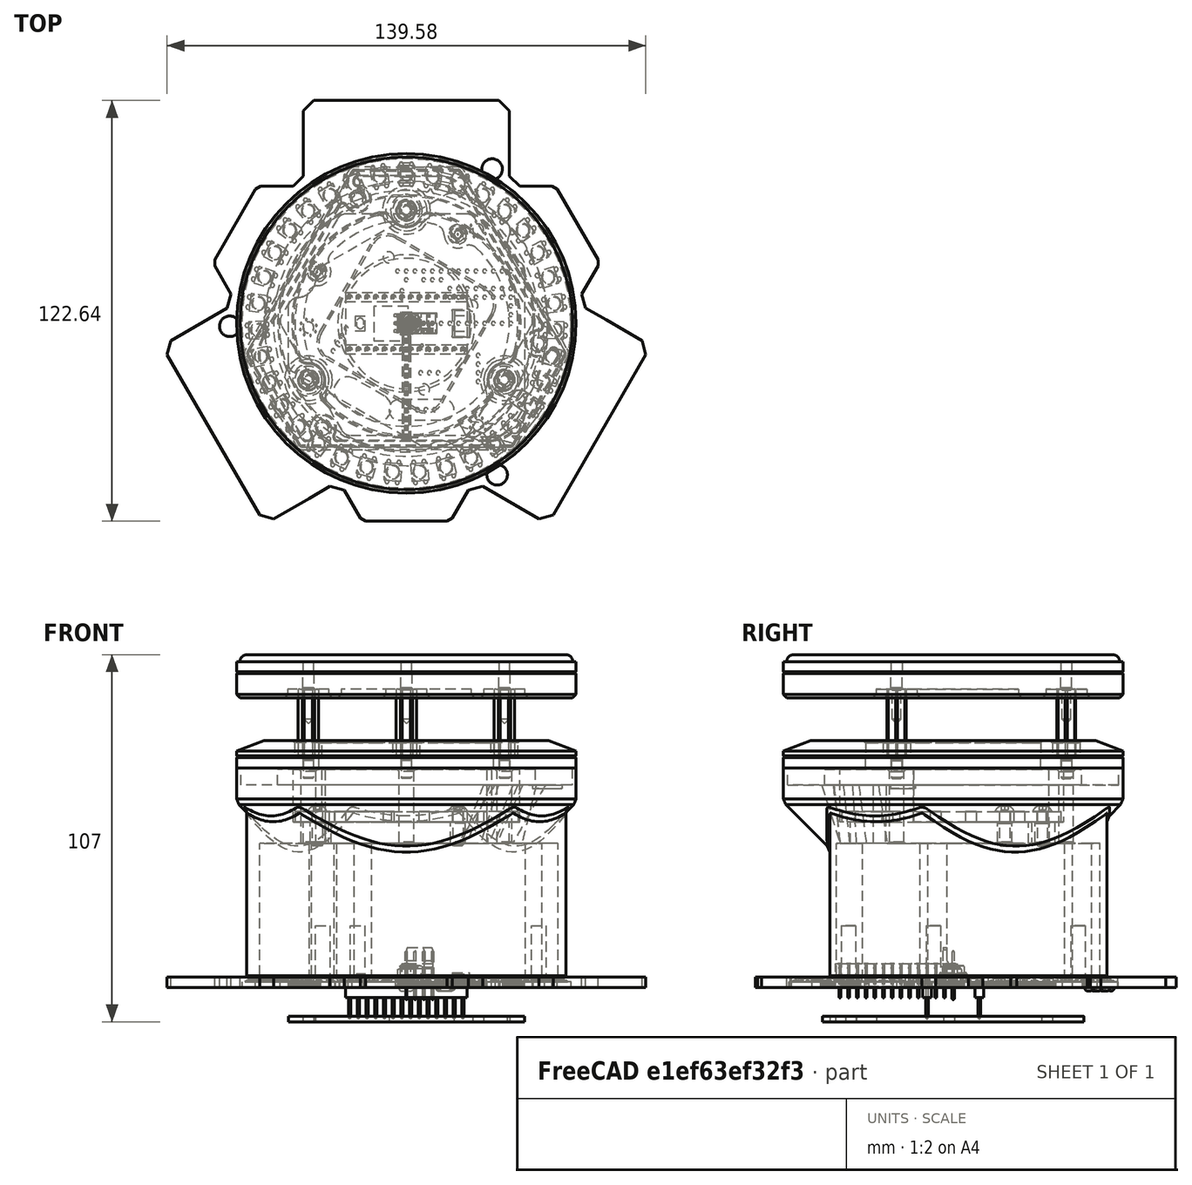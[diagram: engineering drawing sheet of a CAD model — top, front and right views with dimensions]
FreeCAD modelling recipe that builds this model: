
FCSTD DOCUMENT  (FreeCAD 2024.1006R14555 (Git shallow))
Label: beacon_assembled
License: Creative Commons Attribution-NoDerivatives
LicenseURL: http://creativecommons.org/licenses/by-nd/4.0/
objects: Sketcher::SketchObject×35, App::Part×19, PartDesign::Pocket×18, Part::Feature×17, PartDesign::Pad×14, PartDesign::Fillet×14, PartDesign::Chamfer×13, PartDesign::Body×11, Part::FeaturePython×5, PartDesign::PolarPattern×4, PartDesign::SubShapeBinder×4, PartDesign::AuxGroup×3, Part::SubShapeBinder×2, Sketcher::SketchExport×2, App::Link×1, PartDesign::Revolution×1, App::DocumentObjectGroup×1, TechDraw::DrawSVGTemplate×1, TechDraw::DrawProjGroupItem×1, TechDraw::DrawProjGroup×1, +3 more types
note: 307 computed .brp shape members not serialized (recipe doc carries the construction recipe); baked Part::Feature solids carry a one-line shape summary decoded from their .brp
EXTERNAL_REF file=../mechanical-parts/generic-hardware.FCStd obj=Part003
EXTERNAL_REF file=../table_2022.FCStd obj=Group
EXTERNAL_REF file=../robot_holonome.FCStd obj=Part

FEATURE [Sketcher::SketchObject] Sketch
  ArcFitTolerance = 0
  AttachmentSupport = -> [XY_Plane]
  ExternalBSplineMaxDegree = 0
  ExternalBSplineTolerance = 0
  FullyConstrained = true
  InternalTolerance = 1e-06
  InvalidShape = false
  MakeInternals = false
  MapMode = 5
  Support = -> [XY_Plane]
  TreeRank = 0
  ValidateShape = true
  sketch-geometry (17):
    g0: LineSegment StartX=0 StartY=0 StartZ=0 EndX=-49.9177 EndY=28.82 EndZ=0
    g1: LineSegment StartX=-49.9177 StartY=28.82 StartZ=0 EndX=-56.3725 EndY=17.64 EndZ=0
    g2: LineSegment StartX=-56.3725 StartY=17.64 StartZ=0 EndX=-49.641 EndY=5.98076 EndZ=0
    g3: LineSegment StartX=-49.641 StartY=5.98076 StartZ=0 EndX=-58.3013 EndY=0.980762 EndZ=0
    g4: LineSegment [constr] StartX=-58.3013 StartY=0.980762 StartZ=0 EndX=-28.3013 EndY=-50.9808 EndZ=0
    g5: LineSegment StartX=-28.3013 StartY=-50.9808 StartZ=0 EndX=-19.641 EndY=-45.9808 EndZ=0
    g6: LineSegment StartX=-19.641 StartY=-45.9808 StartZ=0 EndX=-12.9096 EndY=-57.64 EndZ=0
    g7: LineSegment StartX=-12.9096 StartY=-57.64 StartZ=0 EndX=0 EndY=-57.64 EndZ=0
    g8: LineSegment StartX=0 StartY=-57.64 StartZ=0 EndX=0 EndY=0 EndZ=0
    g9: LineSegment [constr] StartX=-49.641 StartY=5.98076 StartZ=0 EndX=-19.641 EndY=-45.9808 EndZ=0
    g10: LineSegment [constr] StartX=0 StartY=0 StartZ=0 EndX=-43.3013 EndY=-25 EndZ=0
    g11: LineSegment [constr] StartX=-53.9711 StartY=3.48076 StartZ=0 EndX=-23.9711 EndY=-48.4808 EndZ=0
    g12: Circle CenterX=-51.4711 CenterY=-0.849365 CenterZ=0 NormalX=0 NormalY=0 NormalZ=1 AngleXU=0 Radius=1.6
    g13: Circle [constr] CenterX=-26.4711 CenterY=-44.1506 CenterZ=0 NormalX=0 NormalY=0 NormalZ=1 AngleXU=0 Radius=1.6
    g14: LineSegment StartX=-58.3013 StartY=0.980762 StartZ=0 EndX=-71.2917 EndY=-6.51924 EndZ=0
    g15: LineSegment StartX=-71.2917 StartY=-6.51924 StartZ=0 EndX=-41.2917 EndY=-58.4808 EndZ=0
    g16: LineSegment StartX=-41.2917 StartY=-58.4808 StartZ=0 EndX=-28.3013 EndY=-50.9808 EndZ=0
  constraints (47):
    c: Coincident(g0,g-1)
    c: Coincident(g0,g1)
    c: Coincident(g1,g2)
    c: Coincident(g2,g3)
    c: Coincident(g3,g4)
    c: Coincident(g4,g5)
    c: Coincident(g5,g6)
    c: Coincident(g6,g7)
    c: PointOnObject(g7,g-2)
    c: Horizontal(g7)
    c: Coincident(g7,g8)
    c: Coincident(g8,g0)
    c: Equal(g0,g8)
    c: Angle(g0,g8) = 2.0944
    c: Perpendicular(g0,g1)
    c: Equal(g1,g7)
    c: Perpendicular(g3,g2)
    c: Perpendicular(g3,g4)
    c: Perpendicular(g5,g4)
    c: Coincident(g9,g2)
    c: Coincident(g9,g5)
    c: Coincident(g10,g0)
    c: PointOnObject(g10,g4)
    c: Parallel(g2,g9)
    c: Parallel(g9,g6)
    c: Distance(g4) = 60
    c: Distance(g3) = 10
    c: Perpendicular(g4,g10)
    c: Distance(g0,g9) = 40
    c: PointOnObject(g11,g5)
    c: Symmetric(g3,g2,g11)
    c: PointOnObject(g12,g11)
    c: PointOnObject(g13,g11)
    c: Diameter(g13) = 3.2
    c: Equal(g13,g12)
    c: Symmetric(g13,g12,g10)
    c: Distance(g12,g3) = 5
    c: Coincident(g14,g3)
    c: Coincident(g14,g15)
    c: Coincident(g15,g16)
    c: Coincident(g16,g4)
    c: Parallel(g16,g5)
    c: Parallel(g3,g14)
    c: Parallel(g15,g4)
    c: Distance(g14) = 15
    c: Equal(g6,g2)
    c: DistanceY(g8,g8) = 57.64
FEATURE [PartDesign::Pad] Pad
  AddSubType = 0
  AutoTaperInnerAngle = false
  CheckUpToFaceLimits = true
  ClaimChildren = false
  Direction = (0,0,1)
  Fit = 0
  FitJoin = 0
  InnerFit = 0
  InnerFitJoin = 0
  InvalidShape = false
  Length = 3
  Length2 = 100
  Linearize = true
  NewSolid = false
  Profile = -> Sketch
  Refine = true
  Suppress = false
  TaperInnerAngle = 0
  TaperInnerAngleRev = 0
  TreeRank = 0
  Type = 0
  ValidateShape = true
  _ProfileBasedVersion = 1
FEATURE [PartDesign::PolarPattern] PolarPattern
  AddSubType = 0
  Angle = 360
  Axis = -> Sketch [N_Axis]
  BaseFeature = -> Pad
  CopyShape = false
  HideBaseFeature = false
  InvalidShape = false
  NewSolid = false
  Occurrences = 3
  OffsetBaseFeature = true
  OriginalSubs = -> [Pad]
  Originals = -> [Pad]
  ParallelTransform = true
  Refine = true
  SubTransform = true
  Suppress = false
  TreeRank = 0
  ValidateShape = true
  _Version = 3
FEATURE [Sketcher::SketchObject] Sketch001
  ArcFitTolerance = 0
  AttachmentSupport = -> [XY_Plane]
  ExternalBSplineMaxDegree = 0
  ExternalBSplineTolerance = 0
  ExternalGeometry = -> [PolarPattern]
  FullyConstrained = false
  InternalTolerance = 1e-06
  InvalidShape = false
  MakeInternals = false
  MapMode = 5
  Support = -> [XY_Plane]
  TreeRank = 0
  ValidateShape = true
  sketch-geometry (6):
    g0: LineSegment StartX=-28.2671 StartY=16.32 StartZ=0 EndX=-37.2671 EndY=0.731543 EndZ=0
    g1: LineSegment StartX=-37.2671 StartY=0.731543 StartZ=0 EndX=-18 EndY=-32.64 EndZ=0
    g2: LineSegment StartX=-18 StartY=-32.64 StartZ=0 EndX=0 EndY=-32.64 EndZ=0
    g3: LineSegment StartX=-28.2671 StartY=16.32 StartZ=0 EndX=0 EndY=0 EndZ=0
    g4: LineSegment StartX=0 StartY=0 StartZ=0 EndX=0 EndY=-32.64 EndZ=0
    g5: LineSegment [constr] StartX=0 StartY=0 StartZ=0 EndX=-46.3654 EndY=26.7691 EndZ=0
  constraints (16):
    c: Coincident(g0,g1)
    c: Coincident(g1,g2)
    c: Horizontal(g2)
    c: Equal(g2,g0)
    c: Coincident(g0,g3)
    c: Coincident(g3,g4)
    c: Coincident(g4,g2)
    c: DistanceX(g2,g2) = 18
    c: Coincident(g5,g3)
    c: PointOnObject(g0,g5)
    c: Equal(g3,g4)
    c: Coincident(g3,g-1)
    c: Parallel(g-3,g1)
    c: DistanceY(g-5,g2) = 25
    c: Parallel(g0,g-4)
    c: PointOnObject(g2,g-2)
FEATURE [PartDesign::Pocket] Pocket
  AddSubType = 1
  AutoTaperInnerAngle = false
  BaseFeature = -> PolarPattern
  CheckUpToFaceLimits = true
  ClaimChildren = false
  Direction = (0,0,-1)
  Fit = 0
  FitJoin = 0
  InnerFit = 0
  InnerFitJoin = 0
  InvalidShape = false
  Length = 5
  Length2 = 100
  Linearize = true
  NewSolid = false
  Profile = -> Sketch001
  Refine = true
  Reversed = true
  Suppress = false
  TaperInnerAngle = 0
  TaperInnerAngleRev = 0
  TreeRank = 0
  Type = 1
  ValidateShape = true
  _ProfileBasedVersion = 1
  _Version = 1
FEATURE [PartDesign::PolarPattern] PolarPattern001
  AddSubType = 0
  Angle = 360
  Axis = -> Sketch001 [N_Axis]
  BaseFeature = -> Pocket
  CopyShape = false
  HideBaseFeature = false
  InvalidShape = false
  NewSolid = false
  Occurrences = 3
  OffsetBaseFeature = true
  OriginalSubs = -> [Pocket]
  Originals = -> [Pocket]
  ParallelTransform = true
  Refine = true
  SubTransform = true
  Suppress = false
  TreeRank = 0
  ValidateShape = true
  _Version = 3
FEATURE [PartDesign::Chamfer] Chamfer
  AddSubType = 0
  Angle = 45
  Base = -> PolarPattern001 [Edge67,Edge68,Edge1,Edge6,Edge75,Edge74]
  BaseFeature = -> PolarPattern001
  ChamferType = 0
  FlipDirection = false
  InvalidShape = false
  NewSolid = false
  Refine = true
  Size = 1
  Size2 = 1
  SupportTransform = false
  Suppress = false
  TreeRank = 0
  UseAllEdges = false
  ValidateShape = true
FEATURE [PartDesign::Fillet] Fillet
  AddSubType = 0
  Base = -> Chamfer [Edge98,Edge102,Edge103,Edge101,Edge100,Edge99]
  BaseFeature = -> Chamfer
  InvalidShape = false
  NewSolid = false
  Radius = 3
  Refine = true
  SupportTransform = false
  Suppress = false
  TreeRank = 0
  UseAllEdges = false
  ValidateShape = true
FEATURE [App::Link] Link001  label="Link001(LD06)"
  AutoLinkLabel = true
  AutoPlacement = true
  LinkPlacement = pos=(2.4274e-12,-2.45859e-11,51.3) rot=(0,0,-1;0.523599rad)
  LinkedObject = -> <external ../mechanical-parts/generic-hardware.FCStd>#Part003
  Placement = pos=(2.4274e-12,-2.45859e-11,51.3) rot=(0,0,-1;0.523599rad)
  SyncGroupVisibility = false
  TreeRank = 83
  _LinkVersion = 1
FEATURE [Part::FeaturePython] PcbStandoff  label="M3x5.5x20-Standoff"  # WARN: FeaturePython — macro-defined, semantics opaque (R4)
  Diameter = 2
  InvalidShape = false
  Invert = false
  LeftHanded = false
  Length = 2
  LengthCustom = 20
  MatchOuter = false
  OffsetAngle = 0
  Placement = pos=(-28.5788,-16.5,67) rot=(0,0,1;0rad)
  ScrewLength = 6
  Thread = false
  TreeRank = 174
  Type = 0
  ValidateShape = true
  Width = 1
FEATURE [Part::FeaturePython] PcbStandoff001  label="M3x5.5x20-Standoff001"  # WARN: FeaturePython — macro-defined, semantics opaque (R4)
  Diameter = 2
  InvalidShape = false
  Invert = false
  LeftHanded = false
  Length = 2
  LengthCustom = 20
  MatchOuter = false
  OffsetAngle = 0
  Placement = pos=(28.5788,-16.5,67) rot=(0,0,1;0rad)
  ScrewLength = 6
  Thread = false
  TreeRank = 175
  Type = 0
  ValidateShape = true
  Width = 1
FEATURE [Part::FeaturePython] PcbStandoff002  label="M3x5.5x20-Standoff002"  # WARN: FeaturePython — macro-defined, semantics opaque (R4)
  Diameter = 2
  InvalidShape = false
  Invert = false
  LeftHanded = false
  Length = 2
  LengthCustom = 20
  MatchOuter = false
  OffsetAngle = 0
  Placement = pos=(1.974e-13,33,67) rot=(0,0,1;0rad)
  ScrewLength = 6
  Thread = false
  TreeRank = 176
  Type = 0
  ValidateShape = true
  Width = 1
FEATURE [Sketcher::SketchObject] Sketch042
  ArcFitTolerance = 0
  AttachmentSupport = -> [XY_Plane024]
  ExternalBSplineMaxDegree = 0
  ExternalBSplineTolerance = 0
  FullyConstrained = true
  InternalTolerance = 1e-06
  InvalidShape = false
  MakeInternals = false
  MapMode = 5
  Support = -> [XY_Plane024]
  TreeRank = 402
  ValidateShape = true
  sketch-geometry (9):
    g0: LineSegment StartX=-15.683 StartY=44.8363 StartZ=0 EndX=15.683 EndY=44.8363 EndZ=0
    g1: Circle [constr] CenterX=-4.0211e-12 CenterY=3.5659e-12 CenterZ=0 NormalX=0 NormalY=0 NormalZ=1 AngleXU=0 Radius=47.5
    g2: Circle [constr] CenterX=-4.0211e-12 CenterY=3.5659e-12 CenterZ=0 NormalX=0 NormalY=0 NormalZ=1 AngleXU=0 Radius=36
    g3: LineSegment StartX=-15.683 StartY=44.8363 StartZ=0 EndX=-46.6709 EndY=-8.83631 EndZ=0
    g4: LineSegment StartX=-46.6709 StartY=-8.83631 StartZ=0 EndX=-30.9879 EndY=-36 EndZ=0
    g5: LineSegment StartX=-30.9879 StartY=-36 StartZ=0 EndX=30.9879 EndY=-36 EndZ=0
    g6: LineSegment StartX=30.9879 StartY=-36 StartZ=0 EndX=46.6709 EndY=-8.83631 EndZ=0
    g7: LineSegment StartX=46.6709 StartY=-8.83631 StartZ=0 EndX=15.683 EndY=44.8363 EndZ=0
    g8: LineSegment [constr] StartX=-4.0211e-12 StartY=3.5659e-12 StartZ=0 EndX=-38.8294 EndY=-22.4182 EndZ=0
  constraints (25):
    c: Horizontal(g0)
    c: PointOnObject(g0,g1)
    c: Diameter(g1) = 95
    c: PointOnObject(g0,g1)
    c: Diameter(g2) = 72
    c: Coincident(g3,g0)
    c: PointOnObject(g3,g1)
    c: Coincident(g2,g1)
    c: Coincident(g2,g-1)
    c: Coincident(g4,g3)
    c: PointOnObject(g4,g1)
    c: Coincident(g5,g4)
    c: PointOnObject(g5,g1)
    c: Horizontal(g5)
    c: Coincident(g6,g5)
    c: PointOnObject(g6,g1)
    c: Coincident(g7,g6)
    c: Coincident(g7,g0)
    c: Equal(g0,g4)
    c: Equal(g4,g6)
    c: Equal(g7,g5)
    c: Coincident(g8,g2)
    c: PointOnObject(g8,g4)
    c: Perpendicular(g4,g8)
    c: Tangent(g5,g2)
FEATURE [PartDesign::Pad] Pad026
  AddSubType = 0
  AlongSketchNormal = false
  AutoTaperInnerAngle = false
  CheckUpToFaceLimits = true
  ClaimChildren = false
  Direction = (0,0,1)
  Fit = 0
  FitJoin = 0
  InnerFit = 0
  InnerFitJoin = 0
  InvalidShape = false
  Length = 61
  Length2 = 100
  Linearize = true
  NewSolid = false
  Profile = -> Sketch042
  Refine = true
  Suppress = false
  TaperInnerAngle = 0
  TaperInnerAngleRev = 0
  TreeRank = 403
  Type = 0
  ValidateShape = true
  _ProfileBasedVersion = 1
FEATURE [Sketcher::SketchObject] Sketch043
  ArcFitTolerance = 0
  AttachmentSupport = -> [YZ_Plane024]
  ExternalBSplineMaxDegree = 0
  ExternalBSplineTolerance = 0
  ExternalGeometry = -> [Pad026]
  FullyConstrained = true
  InternalTolerance = 1e-06
  InvalidShape = false
  MakeInternals = false
  MapMode = 5
  Placement = pos=(0,0,0) rot=(0.57735,0.57735,0.57735;2.0944rad)
  Support = -> [YZ_Plane024]
  TreeRank = 404
  ValidateShape = true
  sketch-geometry (5):
    g0: LineSegment StartX=-3.572e-13 StartY=61 StartZ=0 EndX=49.5 EndY=61 EndZ=0
    g1: LineSegment StartX=49.5 StartY=61 StartZ=0 EndX=49.5 EndY=51 EndZ=0
    g2: LineSegment StartX=49.5 StartY=51 StartZ=0 EndX=20 EndY=21.5 EndZ=0
    g3: LineSegment StartX=-2.9e-14 StartY=21.5 StartZ=0 EndX=20 EndY=21.5 EndZ=0
    g4: LineSegment StartX=-2.9e-14 StartY=21.5 StartZ=0 EndX=-3.572e-13 EndY=61 EndZ=0
  constraints (15):
    c: PointOnObject(g0,g-2)
    c: Horizontal(g0)
    c: Coincident(g1,g0)
    c: Coincident(g2,g1)
    c: PointOnObject(g3,g-2)
    c: Coincident(g3,g2)
    c: Horizontal(g3)
    c: Coincident(g4,g0)
    c: Coincident(g3,g4)
    c: Vertical(g1)
    c: PointOnObject(g-3,g0)
    c: DistanceY(g1,g1) = 10
    c: Angle(g1,g2) = 2.35619
    c: DistanceX(g0,g0) = 49.5
    c: DistanceX(g3,g3) = 20
FEATURE [PartDesign::Revolution] Revolution004
  AddSubType = 0
  Angle = 360
  Axis = (-2e-16,3e-16,1)
  Base = (0,0,0)
  BaseFeature = -> Pad026
  ClaimChildren = false
  Fit = 0
  FitJoin = 0
  InnerFit = 0
  InnerFitJoin = 0
  InvalidShape = false
  Linearize = true
  NewSolid = false
  Profile = -> Sketch043
  ReferenceAxis = -> Sketch043 [V_Axis]
  Refine = true
  Reversed = true
  Suppress = false
  TreeRank = 405
  ValidateShape = true
  _ProfileBasedVersion = 1
FEATURE [Sketcher::SketchObject] Sketch044
  ArcFitTolerance = 0
  AttachmentSupport = -> [Revolution004]
  ExternalBSplineMaxDegree = 0
  ExternalBSplineTolerance = 0
  FullyConstrained = true
  InternalTolerance = 1e-06
  InvalidShape = false
  MakeInternals = false
  MapMode = 5
  Placement = pos=(-1.34e-14,1.71e-14,61) rot=(0,0,1;0rad)
  Support = -> [Revolution004]
  TreeRank = 406
  ValidateShape = true
  sketch-geometry (2):
    g0: Circle CenterX=0 CenterY=0 CenterZ=0 NormalX=0 NormalY=0 NormalZ=1 AngleXU=0 Radius=48.25
    g1: Circle CenterX=0 CenterY=0 CenterZ=0 NormalX=0 NormalY=0 NormalZ=1 AngleXU=0 Radius=37.5
  constraints (4):
    c: Coincident(g0,g-1)
    c: Coincident(g1,g0)
    c: Diameter(g0) = 96.5
    c: Diameter(g1) = 75
FEATURE [PartDesign::Pocket] Pocket019
  AddSubType = 1
  AutoTaperInnerAngle = false
  BaseFeature = -> Revolution004
  CheckUpToFaceLimits = true
  ClaimChildren = false
  Direction = (1,1,1)
  Fit = 0
  FitJoin = 0
  InnerFit = 0
  InnerFitJoin = 0
  InvalidShape = false
  Length = 5
  Length2 = 100
  Linearize = true
  NewSolid = false
  Profile = -> Sketch044
  Refine = true
  Suppress = false
  TaperInnerAngle = 0
  TaperInnerAngleRev = 0
  TreeRank = 407
  Type = 0
  ValidateShape = true
  _ProfileBasedVersion = 1
  _Version = 1
FEATURE [Sketcher::SketchObject] Sketch045
  ArcFitTolerance = 0
  AttachmentSupport = -> [Pocket019]
  ExternalBSplineMaxDegree = 0
  ExternalBSplineTolerance = 0
  FullyConstrained = true
  InternalTolerance = 1e-06
  InvalidShape = false
  MakeInternals = false
  MapMode = 5
  Placement = pos=(-1.34e-14,1.71e-14,61) rot=(0,0,1;0rad)
  Support = -> [Pocket019]
  TreeRank = 408
  ValidateShape = true
  sketch-geometry (6):
    g0: Circle CenterX=-6.97e-14 CenterY=33 CenterZ=0 NormalX=0 NormalY=0 NormalZ=1 AngleXU=0 Radius=2.1
    g1: Circle CenterX=28.5788 CenterY=-16.5 CenterZ=0 NormalX=0 NormalY=0 NormalZ=1 AngleXU=0 Radius=2.1
    g2: Circle CenterX=-28.5788 CenterY=-16.5 CenterZ=0 NormalX=0 NormalY=0 NormalZ=1 AngleXU=0 Radius=2.1
    g3: LineSegment [constr] StartX=-28.5788 StartY=-16.5 StartZ=0 EndX=4.26e-14 EndY=-1.279e-13 EndZ=0
    g4: LineSegment [constr] StartX=4.18e-14 StartY=-1.265e-13 StartZ=0 EndX=28.5788 EndY=-16.5 EndZ=0
    g5: LineSegment [constr] StartX=4.18e-14 StartY=-1.265e-13 StartZ=0 EndX=-6.97e-14 EndY=33 EndZ=0
  constraints (15):
    c: PointOnObject(g0,g-2)
    c: Coincident(g3,g2)
    c: Coincident(g3,g-1)
    c: Coincident(g4,g3)
    c: Coincident(g4,g1)
    c: Coincident(g5,g3)
    c: Coincident(g5,g0)
    c: Equal(g2,g1)
    c: Equal(g2,g0)
    c: Diameter(g2) = 4.2
    c: Equal(g3,g4)
    c: Equal(g4,g5)
    c: Angle(g4,g5) = 2.0944
    c: Angle(g5,g3) = 2.0944
    c: DistanceY(g5,g5) = 33
FEATURE [PartDesign::Pocket] Pocket020
  AddSubType = 1
  AutoTaperInnerAngle = false
  BaseFeature = -> Pocket019
  CheckUpToFaceLimits = true
  ClaimChildren = false
  Direction = (1,1,1)
  Fit = 0
  FitJoin = 0
  InnerFit = 0
  InnerFitJoin = 0
  InvalidShape = false
  Length = 12
  Length2 = 100
  Linearize = true
  NewSolid = false
  Profile = -> Sketch045
  Refine = true
  Suppress = false
  TaperInnerAngle = 0
  TaperInnerAngleRev = 0
  TreeRank = 409
  Type = 1
  ValidateShape = true
  _ProfileBasedVersion = 1
  _Version = 1
FEATURE [Sketcher::SketchObject] Sketch046
  ArcFitTolerance = 0
  AttachmentSupport = -> [XY_Plane025]
  ExternalBSplineMaxDegree = 0
  ExternalBSplineTolerance = 0
  FullyConstrained = true
  InternalTolerance = 1e-06
  InvalidShape = false
  MakeInternals = false
  MapMode = 5
  Support = -> [XY_Plane025]
  TreeRank = 422
  ValidateShape = true
  sketch-geometry (12):
    g0: Circle CenterX=-1.6806e-12 CenterY=-6.0018e-12 CenterZ=0 NormalX=0 NormalY=0 NormalZ=1 AngleXU=0 Radius=49.5
    g1: LineSegment StartX=-27.3205 StartY=-7.32051 StartZ=0 EndX=-7.32051 EndY=27.3205 EndZ=0
    g2: LineSegment StartX=-7.32051 StartY=27.3205 StartZ=0 EndX=27.3205 EndY=7.32051 EndZ=0
    g3: LineSegment StartX=27.3205 StartY=7.32051 StartZ=0 EndX=7.32051 EndY=-27.3205 EndZ=0
    g4: LineSegment StartX=7.32051 StartY=-27.3205 StartZ=0 EndX=-27.3205 EndY=-7.32051 EndZ=0
    g5: GeomPoint [constr] X=-1.6806e-12 Y=-6.0018e-12 Z=0
    g6: Circle CenterX=1.962e-13 CenterY=33 CenterZ=0 NormalX=0 NormalY=0 NormalZ=1 AngleXU=0 Radius=1.6
    g7: Circle CenterX=28.5788 CenterY=-16.5 CenterZ=0 NormalX=0 NormalY=0 NormalZ=1 AngleXU=0 Radius=1.6
    g8: Circle CenterX=-28.5788 CenterY=-16.5 CenterZ=0 NormalX=0 NormalY=0 NormalZ=1 AngleXU=0 Radius=1.6
    g9: LineSegment [constr] StartX=-28.5788 StartY=-16.5 StartZ=0 EndX=-1.6804e-12 EndY=-6.0005e-12 EndZ=0
    g10: LineSegment [constr] StartX=-1.6806e-12 StartY=-6.0018e-12 StartZ=0 EndX=28.5788 EndY=-16.5 EndZ=0
    g11: LineSegment [constr] StartX=-1.6806e-12 StartY=-6.0018e-12 StartZ=0 EndX=1.962e-13 EndY=33 EndZ=0
  constraints (29):
    c: Coincident(g0,g-1)
    c: Diameter(g0) = 99
    c: Coincident(g1,g2)
    c: Coincident(g2,g3)
    c: Coincident(g3,g4)
    c: Coincident(g4,g1)
    c: Parallel(g2,g4)
    c: Parallel(g1,g3)
    c: Symmetric(g2,g1,g5)
    c: Coincident(g5,g0)
    c: Perpendicular(g1,g2)
    c: Equal(g3,g2)
    c: Angle(g-2,g4) = 1.0472
    c: Distance(g3) = 40
    c: PointOnObject(g6,g-2)
    c: Equal(g8,g6)
    c: Equal(g8,g7)
    c: Diameter(g8) = 3.2
    c: DistanceY(g0,g6) = 33
    c: Coincident(g9,g8)
    c: Coincident(g9,g0)
    c: Coincident(g10,g0)
    c: Coincident(g10,g7)
    c: Coincident(g11,g0)
    c: Coincident(g11,g6)
    c: Equal(g9,g10)
    c: Equal(g10,g11)
    c: Angle(g10,g11) = 2.0944
    c: Angle(g11,g9) = 2.0944
FEATURE [PartDesign::Pad] Pad027
  AddSubType = 0
  AlongSketchNormal = false
  AutoTaperInnerAngle = false
  CheckUpToFaceLimits = true
  ClaimChildren = false
  Direction = (0,0,1)
  Fit = 0
  FitJoin = 0
  InnerFit = 0
  InnerFitJoin = 0
  InvalidShape = false
  Length = 3
  Length2 = 100
  Linearize = true
  NewSolid = false
  Profile = -> Sketch046
  Refine = true
  Suppress = false
  TaperInnerAngle = 0
  TaperInnerAngleRev = 0
  TreeRank = 423
  Type = 0
  ValidateShape = true
  _ProfileBasedVersion = 1
FEATURE [PartDesign::Fillet] Fillet011
  AddSubType = 0
  Base = -> Pad027 [Edge4,Edge11,Edge8,Edge5]
  BaseFeature = -> Pad027
  InvalidShape = false
  NewSolid = false
  Radius = 5
  Refine = true
  SupportTransform = false
  Suppress = false
  TreeRank = 424
  UseAllEdges = false
  ValidateShape = true
FEATURE [PartDesign::Body] Body024  label="PlaqueDiffuse"
  AutoGroupSolids = false
  ClaimAllChildren = false
  ExportMode = 0
  Group = -> [Sketch046,Pad027,Fillet011]
  InvalidShape = false
  Origin = -> Origin032
  Placement = pos=(0,0,64) rot=(0,0,1;0rad)
  SingleSolid = true
  Tip = -> Fillet011
  TreeRank = 419
  ValidateShape = true
  _ExportChildren = -> [Pad027,Fillet011]
  _GroupVersion = 1
FEATURE [Sketcher::SketchObject] Sketch047
  ArcFitTolerance = 0
  AttachmentSupport = -> [Pocket020]
  ExternalBSplineMaxDegree = 0
  ExternalBSplineTolerance = 0
  ExternalGeometry = -> [Pocket020]
  FullyConstrained = true
  InternalTolerance = 1e-06
  InvalidShape = false
  MakeInternals = false
  MapMode = 5
  Placement = pos=(-1.34e-14,1.71e-14,61) rot=(0,0,1;0rad)
  Support = -> [Pocket020]
  TreeRank = 425
  ValidateShape = true
  sketch-geometry (6):
    g0: ArcOfCircle CenterX=5.9282e-12 CenterY=33 CenterZ=0 NormalX=0 NormalY=0 NormalZ=1 AngleXU=0 Radius=5 StartAngle=3.21742 EndAngle=6.20736
    g1: ArcOfCircle CenterX=-28.5788 CenterY=-16.5 CenterZ=0 NormalX=0 NormalY=0 NormalZ=1 AngleXU=0 Radius=5 StartAngle=5.31182 EndAngle=8.30175
    g2: ArcOfCircle CenterX=28.5788 CenterY=-16.5 CenterZ=0 NormalX=0 NormalY=0 NormalZ=1 AngleXU=0 Radius=5 StartAngle=1.12303 EndAngle=4.11296
    g3: ArcOfCircle CenterX=1.58681e-11 CenterY=6.06976e-11 CenterZ=0 NormalX=0 NormalY=0 NormalZ=1 AngleXU=0 Radius=33 StartAngle=1.72246 EndAngle=3.51353
    g4: ArcOfCircle CenterX=1.58681e-11 CenterY=6.06976e-11 CenterZ=0 NormalX=0 NormalY=0 NormalZ=1 AngleXU=0 Radius=33 StartAngle=5.91125 EndAngle=7.70232
    g5: ArcOfCircle CenterX=1.58681e-11 CenterY=6.06976e-11 CenterZ=0 NormalX=0 NormalY=0 NormalZ=1 AngleXU=0 Radius=33 StartAngle=3.81685 EndAngle=5.60793
  constraints (18):
    c: Coincident(g0,g-3)
    c: Coincident(g1,g-5)
    c: Coincident(g2,g-4)
    c: Coincident(g3,g-1)
    c: Coincident(g3,g1)
    c: Coincident(g3,g0)
    c: Coincident(g4,g3)
    c: Coincident(g4,g0)
    c: Coincident(g4,g2)
    c: Coincident(g5,g3)
    c: Coincident(g5,g1)
    c: Coincident(g5,g2)
    c: Equal(g3,g4)
    c: Equal(g4,g5)
    c: Equal(g0,g2)
    c: Equal(g2,g1)
    c: Radius(g4) = 33
    c: Radius(g2) = 5
FEATURE [PartDesign::Pocket] Pocket021
  AddSubType = 1
  AutoTaperInnerAngle = false
  BaseFeature = -> Pocket020
  CheckUpToFaceLimits = true
  ClaimChildren = false
  Direction = (1,1,1)
  Fit = 0
  FitJoin = 0
  InnerFit = 0
  InnerFitJoin = 0
  InvalidShape = false
  Length = 15.7
  Length2 = 100
  Linearize = true
  NewSolid = false
  Profile = -> Sketch047
  Refine = true
  Suppress = false
  TaperInnerAngle = 0
  TaperInnerAngleRev = 0
  TreeRank = 426
  Type = 0
  ValidateShape = true
  _ProfileBasedVersion = 1
  _Version = 1
FEATURE [PartDesign::Fillet] Fillet012
  AddSubType = 0
  Base = -> Pocket021 [Edge46,Edge43,Edge52,Edge48,Edge50,Edge44]
  BaseFeature = -> Pocket021
  InvalidShape = false
  NewSolid = false
  Radius = 3
  Refine = true
  SupportTransform = false
  Suppress = false
  TreeRank = 427
  UseAllEdges = false
  ValidateShape = true
FEATURE [Sketcher::SketchObject] Sketch049
  ArcFitTolerance = 0
  AttachmentSupport = -> [XY_Plane024]
  ExternalBSplineMaxDegree = 0
  ExternalBSplineTolerance = 0
  FullyConstrained = true
  InternalTolerance = 1e-06
  InvalidShape = false
  MakeInternals = false
  MapMode = 5
  Placement = pos=(0,0,0) rot=(0,1,0;3.14159rad)
  Support = -> [XY_Plane024]
  TreeRank = 451
  ValidateShape = true
FEATURE [Sketcher::SketchObject] Sketch052
  ArcFitTolerance = 0
  AttachmentOffset = pos=(0,0,0) rot=(0,1,0;-2.0944rad)
  AttachmentSupport = -> [XZ_Plane024]
  ExternalBSplineMaxDegree = 0
  ExternalBSplineTolerance = 0
  FullyConstrained = true
  InternalTolerance = 1e-06
  InvalidShape = false
  MakeInternals = false
  MapMode = 5
  Placement = pos=(0,0,0) rot=(-0.377964,0.654654,0.654654;3.86433rad)
  Support = -> [XZ_Plane024]
  TreeRank = 459
  ValidateShape = true
  sketch-geometry (19):
    g0: LineSegment StartX=-18 StartY=5.6 StartZ=0 EndX=-18 EndY=29.4 EndZ=0
    g1: LineSegment StartX=-18 StartY=29.4 StartZ=0 EndX=18 EndY=29.4 EndZ=0
    g2: LineSegment StartX=18 StartY=29.4 StartZ=0 EndX=18 EndY=5.6 EndZ=0
    g3: LineSegment StartX=18 StartY=5.6 StartZ=0 EndX=-18 EndY=5.6 EndZ=0
    g4: GeomPoint [constr] X=-7.1846e-12 Y=17.5 Z=0
    g5: LineSegment [constr] StartX=-15.25 StartY=3.4 StartZ=0 EndX=-15.25 EndY=32.4 EndZ=0
    g6: LineSegment [constr] StartX=-15.25 StartY=32.4 StartZ=0 EndX=15.25 EndY=32.4 EndZ=0
    g7: LineSegment [constr] StartX=15.25 StartY=32.4 StartZ=0 EndX=15.25 EndY=3.4 EndZ=0
    g8: LineSegment [constr] StartX=15.25 StartY=3.4 StartZ=0 EndX=-15.25 EndY=3.4 EndZ=0
    g9: GeomPoint [constr] X=-2.3112e-12 Y=17.9 Z=0
    g10: Circle CenterX=-15.25 CenterY=32.4 CenterZ=0 NormalX=0 NormalY=0 NormalZ=1 AngleXU=0 Radius=1.6
    g11: Circle CenterX=15.25 CenterY=32.4 CenterZ=0 NormalX=0 NormalY=0 NormalZ=1 AngleXU=0 Radius=1.6
    g12: Circle CenterX=15.25 CenterY=3.4 CenterZ=0 NormalX=0 NormalY=0 NormalZ=1 AngleXU=0 Radius=1.6
    g13: Circle CenterX=-15.25 CenterY=3.4 CenterZ=0 NormalX=0 NormalY=0 NormalZ=1 AngleXU=0 Radius=1.6
    g14: LineSegment [constr] StartX=-18 StartY=-2.00412e-11 StartZ=0 EndX=-18 EndY=35 EndZ=0
    g15: LineSegment [constr] StartX=-18 StartY=35 StartZ=0 EndX=18 EndY=35 EndZ=0
    g16: LineSegment [constr] StartX=18 StartY=35 StartZ=0 EndX=18 EndY=-2.00444e-11 EndZ=0
    g17: LineSegment [constr] StartX=18 StartY=-2.00412e-11 StartZ=0 EndX=-18 EndY=-2.00412e-11 EndZ=0
    g18: GeomPoint [constr] X=-7.1846e-12 Y=17.5 Z=0
  constraints (46):
    c: Coincident(g0,g1)
    c: Coincident(g1,g2)
    c: Coincident(g2,g3)
    c: Coincident(g3,g0)
    c: Horizontal(g1)
    c: Horizontal(g3)
    c: Vertical(g0)
    c: Vertical(g2)
    c: Symmetric(g1,g0,g4)
    c: PointOnObject(g4,g-2)
    c: DistanceY(g2,g2) = 23.8
    c: DistanceX(g1,g1) = 36
    c: Coincident(g5,g6)
    c: Coincident(g6,g7)
    c: Coincident(g7,g8)
    c: Coincident(g8,g5)
    c: Horizontal(g6)
    c: Horizontal(g8)
    c: Vertical(g5)
    c: Vertical(g7)
    c: Symmetric(g6,g5,g9)
    c: DistanceX(g6,g6) = 30.5
    c: DistanceY(g7,g7) = 29
    c: PointOnObject(g9,g-2)
    c: DistanceY(g1,g6) = 3
    c: Coincident(g10,g5)
    c: Coincident(g11,g6)
    c: Coincident(g12,g7)
    c: Coincident(g13,g5)
    c: Equal(g13,g12)
    c: Equal(g13,g11)
    c: Equal(g13,g10)
    c: Diameter(g13) = 3.2
    c: Coincident(g14,g15)
    c: Coincident(g15,g16)
    c: Coincident(g16,g17)
    c: Coincident(g17,g14)
    c: Horizontal(g15)
    c: Horizontal(g17)
    c: Vertical(g14)
    c: Vertical(g16)
    c: Symmetric(g15,g14,g18)
    c: Coincident(g18,g4)
    c: DistanceY(g16,g16) = 35
    c: DistanceX(g15,g15) = 36
    c: PointOnObject(g-1,g17)
FEATURE [PartDesign::SubShapeBinder] Binder005  label="Binder005(Chamfer008)"
  BindCopyOnChange = 0
  BindMode = 0
  ClaimChildren = false
  Context = -> <external ../table_2022.FCStd>#Group [Link005.Link014.Body025.Binder005.]
  EdgeTolerance = 1e-06
  FillStyle = 0
  Fuse = false
  InvalidShape = false
  MakeFace = true
  MergeEdges = true
  OffsetFill = false
  OffsetIntersection = false
  OffsetJoinType = 0
  OffsetOpenResult = false
  Outline = false
  PartialLoad = false
  Relative = true
  SplitEdges = false
  Support = -> [Body023[Chamfer008.Face4]]
  TightBound = false
  TreeRank = 479
  ValidateShape = true
  _Version = 8
FEATURE [Sketcher::SketchObject] Sketch053
  ArcFitTolerance = 0
  AttachmentSupport = -> [Binder005]
  ExternalBSplineMaxDegree = 0
  ExternalBSplineTolerance = 0
  FullyConstrained = false
  InternalTolerance = 1e-06
  InvalidShape = false
  MakeInternals = false
  MapMode = 5
  Placement = pos=(0,0,42) rot=(1,0,0;3.14159rad)
  Support = -> [Binder005]
  TreeRank = 480
  ValidateShape = true
  sketch-geometry (18):
    g0: Circle CenterX=-28.5788 CenterY=16.5 CenterZ=0 NormalX=0 NormalY=0 NormalZ=1 AngleXU=0 Radius=1.6
    g1: Circle CenterX=28.5788 CenterY=16.5 CenterZ=0 NormalX=0 NormalY=0 NormalZ=1 AngleXU=0 Radius=1.6
    g2: Circle CenterX=-8.31e-14 CenterY=-33 CenterZ=0 NormalX=0 NormalY=0 NormalZ=1 AngleXU=0 Radius=1.6
    g3: ArcOfCircle CenterX=-24.3484 CenterY=30.5 CenterZ=0 NormalX=0 NormalY=0 NormalZ=1 AngleXU=0 Radius=5.5 StartAngle=3.71693 EndAngle=6.19215
    g4: ArcOfCircle CenterX=38.588 CenterY=5.83631 CenterZ=0 NormalX=0 NormalY=0 NormalZ=1 AngleXU=0 Radius=5.5 StartAngle=1.62253 EndAngle=4.09776
    g5: ArcOfCircle CenterX=-14.2396 CenterY=-36.3363 CenterZ=0 NormalX=0 NormalY=0 NormalZ=1 AngleXU=0 Radius=5.5 StartAngle=5.81132 EndAngle=8.28655
    g6: LineSegment StartX=-16.5452 StartY=-31.3429 StartZ=0 EndX=-39.7427 EndY=8.83631 EndZ=0
    g7: LineSegment StartX=-28.9629 StartY=27.5074 StartZ=0 EndX=-39.7427 EndY=8.83631 EndZ=0
    g8: LineSegment StartX=-18.8711 StartY=30 StartZ=0 EndX=27.5238 EndY=30 EndZ=0
    g9: LineSegment StartX=27.5238 StartY=30 StartZ=0 EndX=38.3035 EndY=11.329 EndZ=0
    g10: LineSegment StartX=35.4163 StartY=1.34289 StartZ=0 EndX=12.2189 EndY=-38.8363 EndZ=0
    g11: LineSegment StartX=12.2189 StartY=-38.8363 StartZ=0 EndX=-9.34061 EndY=-38.8363 EndZ=0
    g12: ArcOfCircle CenterX=-17.6292 CenterY=17.5346 CenterZ=0 NormalX=0 NormalY=0 NormalZ=1 AngleXU=0 Radius=3 StartAngle=2.0944 EndAngle=5.23599
    g13: ArcOfCircle CenterX=-6.37083 CenterY=24.0346 CenterZ=0 NormalX=0 NormalY=0 NormalZ=1 AngleXU=0 Radius=3 StartAngle=5.23599 EndAngle=8.37758
    g14: LineSegment StartX=-16.1292 StartY=14.9365 StartZ=0 EndX=-4.87083 EndY=21.4365 EndZ=0
    g15: LineSegment StartX=-7.87083 StartY=26.6327 StartZ=0 EndX=-19.1292 EndY=20.1327 EndZ=0
    g16: LineSegment [constr] StartX=-17.6292 StartY=17.5346 StartZ=0 EndX=-6.37083 EndY=24.0346 EndZ=0
    g17: LineSegment [constr] StartX=2.367e-13 StartY=4.887e-13 StartZ=0 EndX=-12 EndY=20.7846 EndZ=0
  constraints (35):
    c: Equal(g2,g1)
    c: Equal(g2,g0)
    c: Diameter(g2) = 3.2
    c: Coincident(g6,g5)
    c: Coincident(g7,g3)
    c: Coincident(g7,g6)
    c: Coincident(g8,g3)
    c: Horizontal(g8)
    c: Coincident(g9,g8)
    c: Coincident(g9,g4)
    c: Coincident(g10,g4)
    c: Coincident(g11,g10)
    c: Coincident(g11,g5)
    c: Horizontal(g11)
    c: Equal(g7,g9)
    c: Equal(g8,g6)
    c: Equal(g6,g10)
    c: Radius(g3) = 5.5
    c: Equal(g4,g5)
    c: Equal(g5,g3)
    c: Equal(g11,g9)
    c: Tangent(g12,g14) = -1.5708
    c: Tangent(g14,g13) = -1.5708
    c: Tangent(g13,g15) = -1.5708
    c: Tangent(g15,g12) = -1.5708
    c: Equal(g12,g13)
    c: Angle(g14,g-2) = 1.0472
    c: Distance(g12,g13) = 13
    c: Radius(g13) = 3
    c: Coincident(g16,g12)
    c: Coincident(g16,g13)
    c: Coincident(g17,g-1)
    c: Perpendicular(g16,g17)
    c: Symmetric(g12,g13,g17)
    c: Distance(g17) = 24
FEATURE [PartDesign::Pad] Pad028
  AddSubType = 0
  AlongSketchNormal = false
  AutoTaperInnerAngle = false
  CheckUpToFaceLimits = true
  ClaimChildren = false
  Direction = (0,0,-1)
  Fit = 0
  FitJoin = 0
  InnerFit = 0
  InnerFitJoin = 0
  InvalidShape = false
  Length = 1.6
  Length2 = 100
  Linearize = true
  NewSolid = false
  Profile = -> Sketch053
  Refine = true
  Suppress = false
  TaperInnerAngle = 0
  TaperInnerAngleRev = 0
  TreeRank = 481
  Type = 0
  ValidateShape = true
  _ProfileBasedVersion = 1
FEATURE [PartDesign::Fillet] Fillet017
  AddSubType = 0
  Base = -> Pad028 [Edge2,Edge1,Edge23,Edge20,Edge17,Edge14,Edge11,Edge8,Edge5]
  BaseFeature = -> Pad028
  InvalidShape = false
  NewSolid = false
  Radius = 3
  Refine = true
  SupportTransform = false
  Suppress = false
  TreeRank = 482
  UseAllEdges = false
  ValidateShape = true
FEATURE [PartDesign::Body] Body025  label="ContourPCB"
  AutoGroupSolids = false
  ClaimAllChildren = false
  ExportMode = 0
  Group = -> [Binder005,Sketch053,Pad028,Fillet017]
  InvalidShape = false
  Origin = -> Origin033
  Placement = pos=(4.4049,-1.16633,32) rot=(0.258819,0.965926,0;3.14159rad)
  SingleSolid = true
  Tip = -> Fillet017
  TreeRank = 478
  ValidateShape = true
  _ExportChildren = -> [Binder005,Pad028,Fillet017]
  _GroupVersion = 1
FEATURE [Part::Feature] Part__Feature008  label="SOLID"
  InvalidShape = false
  TreeRank = 540
  ValidateShape = true
  shape: bbox 2.54 x 35.56 x 10.1 mm, 444 faces (baked)
FEATURE [App::Part] PinSocket_1x14_P2_54mm_Vertical  label="PinSocket_1x14_P2.54mm_Vertical"
  ClaimAllChildren = false
  ExportMode = 1
  Group = -> [Part__Feature008]
  Origin = -> Origin034
  Placement = pos=(30.4397,15.3192,1.65) rot=(0,0,-1;1.5708rad)
  TreeRank = 542
  _ExportChildren = -> [Part__Feature008]
  _GroupVersion = 1
FEATURE [Part::Feature] Part__Feature009  label="SOLID"
  InvalidShape = false
  TreeRank = 543
  ValidateShape = true
  shape: bbox 2.54 x 35.56 x 10.1 mm, 444 faces (baked)
FEATURE [App::Part] PinSocket_1x14_P2_54mm_Vertical001  label="PinSocket_1x14_P2.54mm_Vertical"
  ClaimAllChildren = false
  ExportMode = 1
  Group = -> [Part__Feature009]
  Origin = -> Origin035
  Placement = pos=(30.4397,-0.00083,1.65) rot=(0,0,-1;1.5708rad)
  TreeRank = 545
  _ExportChildren = -> [Part__Feature009]
  _GroupVersion = 1
FEATURE [Part::Feature] Part__Feature010  label="SOLID"
  InvalidShape = false
  TreeRank = 546
  ValidateShape = true
  shape: bbox 36.49 x 17.84 x 13.56 mm, 217 faces (baked)
FEATURE [App::Part] Teensy_3_2  label="Teensy_3.2"
  ClaimAllChildren = false
  ExportMode = 1
  Group = -> [Part__Feature010]
  Origin = -> Origin036
  Placement = pos=(13.9397,7.65917,11.65) rot=(0,0,1;3.14159rad)
  TreeRank = 548
  _ExportChildren = -> [Part__Feature010]
  _GroupVersion = 1
FEATURE [Part::Feature] Part__Feature011  label="SOLID"
  InvalidShape = false
  TreeRank = 549
  ValidateShape = true
  shape: bbox 3.2 x 1.6 x 0.55 mm, 26 faces (baked)
FEATURE [App::Part] R_1206_3216Metric
  ClaimAllChildren = false
  ExportMode = 1
  Group = -> [Part__Feature011]
  Origin = -> Origin037
  Placement = pos=(26.7443,-10.6655,1.65) rot=(0,0,-1;1.5708rad)
  TreeRank = 551
  _ExportChildren = -> [Part__Feature011]
  _GroupVersion = 1
FEATURE [Part::Feature] Part__Feature012  label="SOLID"
  InvalidShape = false
  TreeRank = 552
  ValidateShape = true
  shape: bbox 10.16 x 5.8 x 15.26 mm, 117 faces (baked)
FEATURE [App::Part] Molex_KK_254_AE_6410_04A_1x04_P2_54mm_Vertical  label="Molex_KK-254_AE-6410-04A_1x04_P2.54mm_Vertical"
  ClaimAllChildren = false
  ExportMode = 1
  Group = -> [Part__Feature012]
  Origin = -> Origin038
  Placement = pos=(20.9247,-16.9699,1.65) rot=(0,0,1;1.5708rad)
  TreeRank = 554
  _ExportChildren = -> [Part__Feature012]
  _GroupVersion = 1
FEATURE [Part::Feature] Part__Feature013  label="SOLID"
  InvalidShape = false
  TreeRank = 555
  ValidateShape = true
  shape: bbox 9.029 x 9.996 x 8.3 mm, 46 faces (baked)
FEATURE [App::Part] CP_Radial_D6_3mm_P2_50mm  label="CP_Radial_D6.3mm_P2.50mm"
  ClaimAllChildren = false
  ExportMode = 1
  Group = -> [Part__Feature013]
  Origin = -> Origin039
  Placement = pos=(6.72054,-7.69514,1.65) rot=(0,0,1;2.61799rad)
  TreeRank = 557
  _ExportChildren = -> [Part__Feature013]
  _GroupVersion = 1
FEATURE [Part::Feature] Part__Feature014  label="SOLID"
  InvalidShape = false
  TreeRank = 558
  ValidateShape = true
  shape: bbox 11.58 x 8.66 x 5.4 mm, 41 faces (baked)
FEATURE [App::Part] CP_Elec_5x5_4  label="CP_Elec_5x5.4"
  ClaimAllChildren = false
  ExportMode = 1
  Group = -> [Part__Feature014]
  Origin = -> Origin040
  Placement = pos=(-4.16154,-12.2435,1.65) rot=(0,0,1;1.0472rad)
  TreeRank = 560
  _ExportChildren = -> [Part__Feature014]
  _GroupVersion = 1
FEATURE [Part::Feature] Part__Feature015  label="SOLID"
  InvalidShape = false
  TreeRank = 561
  ValidateShape = true
  shape: bbox 3.2 x 1.6 x 1.1 mm, 50 faces (baked)
FEATURE [App::Part] LED_1206_3216Metric
  ClaimAllChildren = false
  ExportMode = 1
  Group = -> [Part__Feature015]
  Origin = -> Origin041
  Placement = pos=(26.7509,-16.242,1.65) rot=(0,0,1;1.5708rad)
  TreeRank = 563
  _ExportChildren = -> [Part__Feature015]
  _GroupVersion = 1
FEATURE [Part::Feature] Part__Feature016  label="SOLID"
  InvalidShape = false
  TreeRank = 564
  ValidateShape = true
  shape: bbox 11.58 x 8.66 x 5.4 mm, 41 faces (baked)
FEATURE [App::Part] CP_Elec_5x5_4001  label="CP_Elec_5x5.4"
  ClaimAllChildren = false
  ExportMode = 1
  Group = -> [Part__Feature016]
  Origin = -> Origin042
  Placement = pos=(-8.60654,-19.9424,1.65) rot=(0,0,1;4.18879rad)
  TreeRank = 566
  _ExportChildren = -> [Part__Feature016]
  _GroupVersion = 1
FEATURE [Part::Feature] Part__Feature017  label="SOLID"
  InvalidShape = false
  TreeRank = 567
  ValidateShape = true
  shape: bbox 8.508 x 9.04 x 1.7 mm, 78 faces (baked)
FEATURE [App::Part] SOT_223  label="SOT-223"
  ClaimAllChildren = false
  ExportMode = 1
  Group = -> [Part__Feature017]
  Origin = -> Origin043
  Placement = pos=(-14.0497,-13.3703,1.65) rot=(0,0,1;2.61799rad)
  TreeRank = 569
  _ExportChildren = -> [Part__Feature017]
  _GroupVersion = 1
FEATURE [Part::Feature] Part__Feature018  label="SOLID"
  InvalidShape = false
  TreeRank = 570
  ValidateShape = true
  shape: bbox 6.703 x 6.325 x 2.22 mm, 41 faces (baked)
FEATURE [App::Part] D_SMA
  ClaimAllChildren = false
  ExportMode = 1
  Group = -> [Part__Feature018]
  Origin = -> Origin044
  Placement = pos=(-10.5497,-7.30815,1.65) rot=(0,0,1;2.61799rad)
  TreeRank = 572
  _ExportChildren = -> [Part__Feature018]
  _GroupVersion = 1
FEATURE [Part::Feature] Part__Feature019  label="SOLID"
  InvalidShape = false
  TreeRank = 573
  ValidateShape = true
  shape: bbox 10.16 x 5.8 x 15.26 mm, 117 faces (baked)
FEATURE [App::Part] Molex_KK_254_AE_6410_04A_1x04_P2_54mm_Vertical001  label="Molex_KK-254_AE-6410-04A_1x04_P2.54mm_Vertical"
  ClaimAllChildren = false
  ExportMode = 1
  Group = -> [Part__Feature019]
  Origin = -> Origin045
  Placement = pos=(-21.344,-8.0043,1.65) rot=(0,0,1;1.0472rad)
  TreeRank = 575
  _ExportChildren = -> [Part__Feature019]
  _GroupVersion = 1
FEATURE [Part::Feature] Part__Feature020  label="SOLID"
  InvalidShape = false
  TreeRank = 576
  ValidateShape = true
  shape: bbox 3.2 x 1.6 x 0.55 mm, 26 faces (baked)
FEATURE [App::Part] R_1206_3216Metric001  label="R_1206_3216Metric"
  ClaimAllChildren = false
  ExportMode = 1
  Group = -> [Part__Feature020]
  Origin = -> Origin046
  Placement = pos=(-10.9749,1.95551,1.65) rot=(0,0,1;2.61799rad)
  TreeRank = 578
  _ExportChildren = -> [Part__Feature020]
  _GroupVersion = 1
FEATURE [Part::Feature] Part__Feature021  label="SOLID"
  InvalidShape = false
  TreeRank = 579
  ValidateShape = true
  shape: bbox 3.2 x 1.6 x 0.55 mm, 26 faces (baked)
FEATURE [App::Part] R_1206_3216Metric002  label="R_1206_3216Metric"
  ClaimAllChildren = false
  ExportMode = 1
  Group = -> [Part__Feature021]
  Origin = -> Origin047
  Placement = pos=(-12.2299,-0.218213,1.65) rot=(0,0,1;2.61799rad)
  TreeRank = 581
  _ExportChildren = -> [Part__Feature021]
  _GroupVersion = 1
FEATURE [Part::Feature] Part__Feature022  label="SOLID"
  InvalidShape = false
  TreeRank = 582
  ValidateShape = true
  shape: bbox 7.62 x 5.8 x 15.26 mm, 91 faces (baked)
FEATURE [App::Part] Molex_KK_254_AE_6410_03A_1x03_P2_54mm_Vertical  label="Molex_KK-254_AE-6410-03A_1x03_P2.54mm_Vertical"
  ClaimAllChildren = false
  ExportMode = 1
  Group = -> [Part__Feature022]
  Origin = -> Origin048
  Placement = pos=(4.19504,-14.4293,-0.05) rot=(1,0,0;3.14159rad)
  TreeRank = 584
  _ExportChildren = -> [Part__Feature022]
  _GroupVersion = 1
FEATURE [Part::Feature] Part__Feature023  label="SOLID"
  InvalidShape = false
  TreeRank = 585
  ValidateShape = true
  shape: bbox 10.16 x 5.8 x 15.26 mm, 117 faces (baked)
FEATURE [App::Part] Molex_KK_254_AE_6410_04A_1x04_P2_54mm_Vertical002  label="Molex_KK-254_AE-6410-04A_1x04_P2.54mm_Vertical"
  ClaimAllChildren = false
  ExportMode = 1
  Group = -> [Part__Feature023]
  Origin = -> Origin049
  Placement = pos=(0.640674,-25.1547,-0.05) rot=(1,0,0;3.14159rad)
  TreeRank = 587
  _ExportChildren = -> [Part__Feature023]
  _GroupVersion = 1
FEATURE [Part::Feature] Part__Feature024  label="MatDetection-2023 PCB"
  InvalidShape = false
  TreeRank = 588
  ValidateShape = true
  shape: bbox 68.84 x 76.19 x 1.6 mm, 426 faces (baked)
FEATURE [App::Part] MatDetection_2023_1  label="LidarBoard-2023"
  ClaimAllChildren = false
  ExportMode = 1
  Group = -> [PinSocket_1x14_P2_54mm_Vertical,PinSocket_1x14_P2_54mm_Vertical001,Teensy_3_2,R_1206_3216Metric,Molex_KK_254_AE_6410_04A_1x04_P2_54mm_Vertical,CP_Radial_D6_3mm_P2_50mm,CP_Elec_5x5_4,LED_1206_3216Metric,CP_Elec_5x5_4001,SOT_223,D_SMA,Molex_KK_254_AE_6410_04A_1x04_P2_54mm_Vertical001,R_1206_3216Metric001,R_1206_3216Metric002,Molex_KK_254_AE_6410_03A_1x03_P2_54mm_Vertical,+3 more]
  Origin = -> Origin050
  Placement = pos=(4.39792,-1.19238,22) rot=(0.258819,0.965926,0;3.14159rad)
  TreeRank = 590
  _ExportChildren = -> [PinSocket_1x14_P2_54mm_Vertical,PinSocket_1x14_P2_54mm_Vertical001,Teensy_3_2,R_1206_3216Metric,Molex_KK_254_AE_6410_04A_1x04_P2_54mm_Vertical,CP_Radial_D6_3mm_P2_50mm,CP_Elec_5x5_4,LED_1206_3216Metric,CP_Elec_5x5_4001,SOT_223,D_SMA,Molex_KK_254_AE_6410_04A_1x04_P2_54mm_Vertical001,R_1206_3216Metric001,R_1206_3216Metric002,Molex_KK_254_AE_6410_03A_1x03_P2_54mm_Vertical,+3 more]
  _GroupVersion = 1
FEATURE [Sketcher::SketchObject] Sketch054
  ArcFitTolerance = 1e-06
  AttachmentSupport = -> [XY_Plane028]
  ExternalBSplineMaxDegree = 0
  ExternalBSplineTolerance = 0
  FullyConstrained = true
  InternalTolerance = 1e-06
  InvalidShape = false
  MakeInternals = false
  MapMode = 5
  Support = -> [XY_Plane028]
  TreeRank = 614
  ValidateShape = true
  sketch-geometry (2):
    g0: Circle CenterX=0 CenterY=0 CenterZ=0 NormalX=0 NormalY=0 NormalZ=1 AngleXU=0 Radius=48
    g1: Circle CenterX=0 CenterY=0 CenterZ=0 NormalX=0 NormalY=0 NormalZ=1 AngleXU=0 Radius=38.75
  constraints (4):
    c: Diameter(g1) = 77.5
    c: Diameter(g0) = 96
    c: Coincident(g1,g-1)
    c: Coincident(g0,g1)
FEATURE [PartDesign::Pad] Pad029
  AddSubType = 0
  AlongSketchNormal = false
  AutoTaperInnerAngle = false
  CheckUpToFaceLimits = true
  ClaimChildren = false
  Direction = (0,0,1)
  Fit = 0
  FitJoin = 0
  InnerFit = 0
  InnerFitJoin = 0
  InvalidShape = false
  Length = 1.6
  Length2 = 100
  Linearize = true
  NewSolid = false
  Profile = -> Sketch054
  Refine = true
  Suppress = false
  TaperInnerAngle = 0
  TaperInnerAngleRev = 0
  TreeRank = 615
  Type = 0
  ValidateShape = true
  _ProfileBasedVersion = 1
FEATURE [Sketcher::SketchObject] Sketch055
  ArcFitTolerance = 1e-06
  AttachmentSupport = -> [XY_Plane028]
  ExternalBSplineMaxDegree = 0
  ExternalBSplineTolerance = 0
  FullyConstrained = true
  InternalTolerance = 1e-06
  InvalidShape = false
  MakeInternals = false
  MapMode = 5
  Placement = pos=(0,0,0) rot=(0,1,0;3.14159rad)
  Support = -> [XY_Plane028]
  TreeRank = 616
  ValidateShape = true
  sketch-geometry (28):
    g0: ArcOfCircle CenterX=-1.3 CenterY=46.04 CenterZ=0 NormalX=0 NormalY=0 NormalZ=1 AngleXU=0 Radius=0.9 StartAngle=1.5708 EndAngle=4.71239
    g1: ArcOfCircle CenterX=1.3 CenterY=46.04 CenterZ=0 NormalX=0 NormalY=0 NormalZ=1 AngleXU=0 Radius=0.9 StartAngle=4.71239 EndAngle=7.85398
    g2: LineSegment StartX=-1.3 StartY=45.14 StartZ=0 EndX=1.3 EndY=45.14 EndZ=0
    g3: LineSegment StartX=1.3 StartY=46.94 StartZ=0 EndX=-1.3 EndY=46.94 EndZ=0
    g4: ArcOfCircle CenterX=-1.3 CenterY=43.5 CenterZ=0 NormalX=0 NormalY=0 NormalZ=1 AngleXU=0 Radius=0.9 StartAngle=1.5708 EndAngle=4.71239
    g5: ArcOfCircle CenterX=1.3 CenterY=43.5 CenterZ=0 NormalX=0 NormalY=0 NormalZ=1 AngleXU=0 Radius=0.9 StartAngle=4.71239 EndAngle=7.85398
    g6: LineSegment StartX=-1.3 StartY=42.6 StartZ=0 EndX=1.3 EndY=42.6 EndZ=0
    g7: LineSegment StartX=1.3 StartY=44.4 StartZ=0 EndX=-1.3 EndY=44.4 EndZ=0
    g8: ArcOfCircle CenterX=-1.3 CenterY=40.96 CenterZ=0 NormalX=0 NormalY=0 NormalZ=1 AngleXU=0 Radius=0.9 StartAngle=1.5708 EndAngle=4.71239
    g9: ArcOfCircle CenterX=1.3 CenterY=40.96 CenterZ=0 NormalX=0 NormalY=0 NormalZ=1 AngleXU=0 Radius=0.9 StartAngle=4.71239 EndAngle=7.85398
    g10: LineSegment StartX=-1.3 StartY=40.06 StartZ=0 EndX=1.3 EndY=40.06 EndZ=0
    g11: LineSegment StartX=1.3 StartY=41.86 StartZ=0 EndX=-1.3 EndY=41.86 EndZ=0
    g12: ArcOfCircle CenterX=-13.1668 CenterY=44.2127 CenterZ=0 NormalX=0 NormalY=0 NormalZ=1 AngleXU=0 Radius=0.9 StartAngle=1.80385 EndAngle=4.94544
    g13: ArcOfCircle CenterX=-10.6371 CenterY=44.8132 CenterZ=0 NormalX=0 NormalY=0 NormalZ=1 AngleXU=0 Radius=0.9 StartAngle=4.94544 EndAngle=8.08703
    g14: LineSegment StartX=-12.959 StartY=43.3371 StartZ=0 EndX=-10.4293 EndY=43.9375 EndZ=0
    g15: LineSegment StartX=-10.845 StartY=45.6889 StartZ=0 EndX=-13.3747 EndY=45.0884 EndZ=0
    g16: ArcOfCircle CenterX=-12.5805 CenterY=41.7425 CenterZ=0 NormalX=0 NormalY=0 NormalZ=1 AngleXU=0 Radius=0.9 StartAngle=1.80385 EndAngle=4.94544
    g17: ArcOfCircle CenterX=-10.0508 CenterY=42.343 CenterZ=0 NormalX=0 NormalY=0 NormalZ=1 AngleXU=0 Radius=0.9 StartAngle=4.94544 EndAngle=8.08703
    g18: LineSegment StartX=-12.3726 StartY=40.8668 StartZ=0 EndX=-9.84292 EndY=41.4673 EndZ=0
    g19: LineSegment StartX=-10.2586 StartY=43.2186 StartZ=0 EndX=-12.7883 EndY=42.6182 EndZ=0
    g20: ArcOfCircle CenterX=-11.9941 CenterY=39.2723 CenterZ=0 NormalX=0 NormalY=0 NormalZ=1 AngleXU=0 Radius=0.9 StartAngle=1.80385 EndAngle=4.94544
    g21: ArcOfCircle CenterX=-9.46443 CenterY=39.8727 CenterZ=0 NormalX=0 NormalY=0 NormalZ=1 AngleXU=0 Radius=0.9 StartAngle=4.94544 EndAngle=8.08703
    g22: LineSegment StartX=-11.7863 StartY=38.3966 StartZ=0 EndX=-9.25658 EndY=38.9971 EndZ=0
    g23: LineSegment StartX=-9.67228 StartY=40.7484 StartZ=0 EndX=-12.202 EndY=40.148 EndZ=0
    g24: LineSegment [constr] StartX=-10.6371 StartY=44.8132 StartZ=0 EndX=0 EndY=0 EndZ=0
    g25: LineSegment [constr] StartX=-12.5805 StartY=41.7425 StartZ=0 EndX=-10.0508 EndY=42.343 EndZ=0
    g26: Circle [constr] CenterX=0 CenterY=0 CenterZ=0 NormalX=0 NormalY=0 NormalZ=1 AngleXU=0 Radius=46.0583
    g27: Circle [constr] CenterX=0 CenterY=0 CenterZ=0 NormalX=0 NormalY=0 NormalZ=1 AngleXU=0 Radius=40.9806
  constraints (65):
    c: Tangent(g0,g2) = -1.5708
    c: Tangent(g2,g1) = -1.5708
    c: Tangent(g1,g3) = -1.5708
    c: Tangent(g3,g0) = -1.5708
    c: Equal(g0,g1)
    c: Tangent(g4,g6) = -1.5708
    c: Tangent(g6,g5) = -1.5708
    c: Tangent(g5,g7) = -1.5708
    c: Tangent(g7,g4) = -1.5708
    c: Equal(g4,g5)
    c: Tangent(g8,g10) = -1.5708
    c: Tangent(g10,g9) = -1.5708
    c: Tangent(g9,g11) = -1.5708
    c: Tangent(g11,g8) = -1.5708
    c: Equal(g8,g9)
    c: Equal(g2,g11)
    c: Equal(g11,g6)
    c: Horizontal(g7)
    c: Horizontal(g11)
    c: Equal(g0,g4)
    c: Equal(g4,g8)
    c: Symmetric(g0,g1,g-2)
    c: Vertical(g1,g5)
    c: Radius(g1) = 0.9
    c: Symmetric(g9,g1,g5)
    c: DistanceX(g0,g1) = 2.6
    c: DistanceY(g-1,g5) = 43.5
    c: DistanceY(g9,g1) = 5.08
    c: Tangent(g12,g14) = -1.5708
    c: Tangent(g14,g13) = -1.5708
    c: Tangent(g13,g15) = -1.5708
    c: Tangent(g15,g12) = -1.5708
    c: Equal(g12,g13)
    c: Tangent(g16,g18) = -1.5708
    c: Tangent(g18,g17) = -1.5708
    c: Tangent(g17,g19) = -1.5708
    c: Tangent(g19,g16) = -1.5708
    c: Equal(g16,g17)
    c: Tangent(g20,g22) = -1.5708
    c: Tangent(g22,g21) = -1.5708
    c: Tangent(g21,g23) = -1.5708
    c: Tangent(g23,g20) = -1.5708
    c: Equal(g20,g21)
    c: Equal(g21,g17)
    c: Equal(g17,g13)
    c: Equal(g13,g4)
    c: Equal(g14,g19)
    c: Equal(g19,g23)
    c: Equal(g23,g11)
    c: PointOnObject(g17,g24)
    c: Parallel(g23,g18)
    c: Parallel(g18,g14)
    c: Perpendicular(g24,g25)
    c: Coincident(g25,g17)
    c: Coincident(g16,g25)
    c: Coincident(g13,g24)
    c: PointOnObject(g13,g26)
    c: Coincident(g26,g24)
    c: Coincident(g26,g-1)
    c: PointOnObject(g0,g26)
    c: Symmetric(g21,g13,g17)
    c: PointOnObject(g8,g27)
    c: PointOnObject(g21,g27)
    c: Coincident(g27,g24)
    c: Distance(g13,g1) = 12
FEATURE [PartDesign::Pad] Pad030
  AddSubType = 0
  AlongSketchNormal = false
  AutoTaperInnerAngle = false
  BaseFeature = -> Pad029
  CheckUpToFaceLimits = true
  ClaimChildren = false
  Direction = (0,0,-1)
  Fit = 0
  FitJoin = 0
  InnerFit = 0
  InnerFitJoin = 0
  InvalidShape = false
  Length = 1
  Length2 = 100
  Linearize = true
  NewSolid = false
  Profile = -> Sketch055
  Refine = true
  Suppress = false
  TaperInnerAngle = 0
  TaperInnerAngleRev = 0
  TreeRank = 617
  Type = 0
  ValidateShape = true
  _ProfileBasedVersion = 1
FEATURE [PartDesign::Fillet] Fillet018
  AddSubType = 0
  Base = -> Pad030 [Edge75,Edge67,Edge59,Edge35,Edge43,Edge51]
  BaseFeature = -> Pad030
  InvalidShape = false
  NewSolid = false
  Radius = 0.8
  Refine = true
  SupportTransform = false
  Suppress = false
  TreeRank = 618
  UseAllEdges = false
  ValidateShape = true
FEATURE [Sketcher::SketchObject] Sketch056
  ArcFitTolerance = 1e-06
  AttachmentSupport = -> [XY_Plane029]
  ExternalBSplineMaxDegree = 0
  ExternalBSplineTolerance = 0
  FullyConstrained = true
  InternalTolerance = 1e-06
  InvalidShape = false
  MakeInternals = false
  MapMode = 5
  Support = -> [XY_Plane029]
  TreeRank = 619
  ValidateShape = true
  sketch-geometry (5):
    g0: LineSegment StartX=-2.5 StartY=46 StartZ=0 EndX=-2.5 EndY=41 EndZ=0
    g1: LineSegment StartX=-2.5 StartY=41 StartZ=0 EndX=2.5 EndY=41 EndZ=0
    g2: LineSegment StartX=2.5 StartY=41 StartZ=0 EndX=2.5 EndY=46 EndZ=0
    g3: LineSegment StartX=2.5 StartY=46 StartZ=0 EndX=-2.5 EndY=46 EndZ=0
    g4: GeomPoint [constr] X=-3.2055e-12 Y=43.5 Z=0
  constraints (13):
    c: Coincident(g0,g1)
    c: Coincident(g1,g2)
    c: Coincident(g2,g3)
    c: Coincident(g3,g0)
    c: Horizontal(g1)
    c: Horizontal(g3)
    c: Vertical(g0)
    c: Vertical(g2)
    c: Symmetric(g1,g0,g4)
    c: PointOnObject(g4,g-2)
    c: Equal(g3,g2)
    c: DistanceX(g3,g3) = 5
    c: DistanceY(g4) = 43.5
FEATURE [PartDesign::Pad] Pad031
  AddSubType = 0
  AlongSketchNormal = false
  AutoTaperInnerAngle = false
  CheckUpToFaceLimits = true
  ClaimChildren = false
  Direction = (0,0,1)
  Fit = 0
  FitJoin = 0
  InnerFit = 0
  InnerFitJoin = 0
  InvalidShape = false
  Length = 1.4
  Length2 = 100
  Linearize = true
  NewSolid = false
  Profile = -> Sketch056
  Refine = true
  Suppress = false
  TaperInnerAngle = 0
  TaperInnerAngleRev = 0
  TreeRank = 620
  Type = 0
  ValidateShape = true
  _ProfileBasedVersion = 1
FEATURE [Sketcher::SketchObject] Sketch057
  ArcFitTolerance = 1e-06
  AttachmentSupport = -> [Pad031]
  ExternalBSplineMaxDegree = 0
  ExternalBSplineTolerance = 0
  ExternalGeometry = -> [Pad031]
  FullyConstrained = true
  InternalTolerance = 1e-06
  InvalidShape = false
  MakeInternals = false
  MapMode = 5
  Placement = pos=(0,0,1.4) rot=(0,0,1;0rad)
  Support = -> [Pad031]
  TreeRank = 621
  ValidateShape = true
  sketch-geometry (2):
    g0: Circle CenterX=-7.43e-14 CenterY=43.5 CenterZ=0 NormalX=0 NormalY=0 NormalZ=1 AngleXU=0 Radius=2
    g1: LineSegment [constr] StartX=-2.5 StartY=41 StartZ=0 EndX=2.5 EndY=46 EndZ=0
  constraints (5):
    c: PointOnObject(g0,g-2)
    c: Diameter(g0) = 4
    c: Coincident(g1,g-4)
    c: Coincident(g1,g-3)
    c: PointOnObject(g0,g1)
FEATURE [PartDesign::Pocket] Pocket027
  AddSubType = 1
  AutoTaperInnerAngle = false
  BaseFeature = -> Pad031
  CheckUpToFaceLimits = true
  ClaimChildren = false
  Direction = (1,1,1)
  Fit = 0
  FitJoin = 0
  InnerFit = 0
  InnerFitJoin = 0
  InvalidShape = false
  Length = 0.4
  Length2 = 100
  Linearize = true
  NewSolid = false
  Profile = -> Sketch057
  Refine = true
  Suppress = false
  TaperAngle = -30
  TaperInnerAngle = 0
  TaperInnerAngleRev = 0
  TreeRank = 622
  Type = 0
  ValidateShape = true
  _ProfileBasedVersion = 1
  _Version = 1
FEATURE [Sketcher::SketchObject] Sketch058
  ArcFitTolerance = 1e-06
  AttachmentSupport = -> [Pocket027]
  ExternalBSplineMaxDegree = 0
  ExternalBSplineTolerance = 0
  ExternalGeometry = -> [Pocket027]
  FullyConstrained = true
  InternalTolerance = 1e-06
  InvalidShape = false
  MakeInternals = false
  MapMode = 5
  Placement = pos=(0,0,1.4) rot=(0,0,1;0rad)
  Support = -> [Pocket027]
  TreeRank = 623
  ValidateShape = true
  sketch-geometry (3):
    g0: LineSegment StartX=2.5 StartY=46 StartZ=0 EndX=1.5 EndY=46 EndZ=0
    g1: LineSegment StartX=1.5 StartY=46 StartZ=0 EndX=2.5 EndY=45 EndZ=0
    g2: LineSegment StartX=2.5 StartY=45 StartZ=0 EndX=2.5 EndY=46 EndZ=0
  constraints (8):
    c: Coincident(g0,g-4)
    c: PointOnObject(g0,g-3)
    c: Coincident(g1,g0)
    c: PointOnObject(g1,g-4)
    c: Coincident(g2,g0)
    c: Equal(g2,g0)
    c: Coincident(g2,g1)
    c: DistanceX(g0,g0) = 1
FEATURE [PartDesign::Pocket] Pocket028
  AddSubType = 1
  AutoTaperInnerAngle = false
  BaseFeature = -> Pocket027
  CheckUpToFaceLimits = true
  ClaimChildren = false
  Direction = (1,1,1)
  Fit = 0
  FitJoin = 0
  InnerFit = 0
  InnerFitJoin = 0
  InvalidShape = false
  Length = 0.2
  Length2 = 100
  Linearize = true
  NewSolid = false
  Profile = -> Sketch058
  Refine = true
  Suppress = false
  TaperInnerAngle = 0
  TaperInnerAngleRev = 0
  TreeRank = 624
  Type = 0
  ValidateShape = true
  _ProfileBasedVersion = 1
  _Version = 1
FEATURE [Sketcher::SketchObject] Sketch059
  ArcFitTolerance = 1e-06
  AttachmentSupport = -> [XY_Plane029]
  ExternalBSplineMaxDegree = 0
  ExternalBSplineTolerance = 0
  ExternalGeometry = -> [Pocket028]
  FullyConstrained = true
  InternalTolerance = 1e-06
  InvalidShape = false
  MakeInternals = false
  MapMode = 5
  Support = -> [XY_Plane029]
  TreeRank = 625
  ValidateShape = true
  sketch-geometry (17):
    g0: ArcOfCircle CenterX=-1.5 CenterY=46 CenterZ=0 NormalX=0 NormalY=0 NormalZ=1 AngleXU=0 Radius=0.6 StartAngle=3.14159 EndAngle=6.28319
    g1: ArcOfCircle CenterX=-1.5 CenterY=46.4 CenterZ=0 NormalX=0 NormalY=0 NormalZ=1 AngleXU=0 Radius=0.6 StartAngle=1.18506e-11 EndAngle=3.14159
    g2: LineSegment StartX=-0.9 StartY=46 StartZ=0 EndX=-0.9 EndY=46.4 EndZ=0
    g3: LineSegment StartX=-2.1 StartY=46.4 StartZ=0 EndX=-2.1 EndY=46 EndZ=0
    g4: ArcOfCircle CenterX=1.5 CenterY=46 CenterZ=0 NormalX=0 NormalY=0 NormalZ=1 AngleXU=0 Radius=0.6 StartAngle=3.14159 EndAngle=6.28319
    g5: ArcOfCircle CenterX=1.5 CenterY=46.4 CenterZ=0 NormalX=0 NormalY=0 NormalZ=1 AngleXU=0 Radius=0.6 StartAngle=1.68801e-10 EndAngle=3.14159
    g6: LineSegment StartX=2.1 StartY=46 StartZ=0 EndX=2.1 EndY=46.4 EndZ=0
    g7: LineSegment StartX=0.9 StartY=46.4 StartZ=0 EndX=0.9 EndY=46 EndZ=0
    g8: ArcOfCircle CenterX=-1.5 CenterY=41 CenterZ=0 NormalX=0 NormalY=0 NormalZ=1 AngleXU=0 Radius=0.6 StartAngle=-6.253e-13 EndAngle=3.14159
    g9: ArcOfCircle CenterX=-1.5 CenterY=40.6 CenterZ=0 NormalX=0 NormalY=0 NormalZ=1 AngleXU=0 Radius=0.6 StartAngle=3.14159 EndAngle=6.28319
    g10: LineSegment StartX=-2.1 StartY=41 StartZ=0 EndX=-2.1 EndY=40.6 EndZ=0
    g11: LineSegment StartX=-0.9 StartY=40.6 StartZ=0 EndX=-0.9 EndY=41 EndZ=0
    g12: ArcOfCircle CenterX=1.5 CenterY=41 CenterZ=0 NormalX=0 NormalY=0 NormalZ=1 AngleXU=0 Radius=0.6 StartAngle=1.31086e-10 EndAngle=3.14159
    g13: ArcOfCircle CenterX=1.5 CenterY=40.6 CenterZ=0 NormalX=0 NormalY=0 NormalZ=1 AngleXU=0 Radius=0.6 StartAngle=3.14159 EndAngle=6.28319
    g14: LineSegment StartX=0.9 StartY=41 StartZ=0 EndX=0.9 EndY=40.6 EndZ=0
    g15: LineSegment StartX=2.1 StartY=40.6 StartZ=0 EndX=2.1 EndY=41 EndZ=0
    g16: LineSegment [constr] StartX=-1.5 StartY=40 StartZ=0 EndX=-1.5 EndY=47 EndZ=0
  constraints (41):
    c: Tangent(g0,g2) = -1.5708
    c: Tangent(g2,g1) = -1.5708
    c: Tangent(g1,g3) = -1.5708
    c: Tangent(g3,g0) = -1.5708
    c: Equal(g0,g1)
    c: PointOnObject(g0,g-4)
    c: Tangent(g4,g6) = -1.5708
    c: Tangent(g6,g5) = -1.5708
    c: Tangent(g5,g7) = -1.5708
    c: Tangent(g7,g4) = -1.5708
    c: Equal(g4,g5)
    c: Tangent(g8,g10) = -1.5708
    c: Tangent(g10,g9) = -1.5708
    c: Tangent(g9,g11) = -1.5708
    c: Tangent(g11,g8) = -1.5708
    c: Equal(g8,g9)
    c: Tangent(g12,g14) = -1.5708
    c: Tangent(g14,g13) = -1.5708
    c: Tangent(g13,g15) = -1.5708
    c: Tangent(g15,g12) = -1.5708
    c: Equal(g12,g13)
    c: Equal(g1,g5)
    c: Equal(g5,g13)
    c: Equal(g13,g9)
    c: Equal(g11,g14)
    c: Equal(g14,g7)
    c: Equal(g7,g2)
    c: Vertical(g2)
    c: Vertical(g11)
    c: Vertical(g14)
    c: Vertical(g7)
    c: Symmetric(g0,g4,g-2)
    c: Symmetric(g8,g12,g-2)
    c: Symmetric(g0,g12,g-5)
    c: PointOnObject(g16,g9)
    c: PointOnObject(g16,g1)
    c: Vertical(g16)
    c: PointOnObject(g1,g16)
    c: DistanceY(g16,g16) = 7
    c: Radius(g1) = 0.6
    c: DistanceX(g1,g5) = 3
FEATURE [PartDesign::Pad] Pad032
  AddSubType = 0
  AlongSketchNormal = false
  AutoTaperInnerAngle = false
  BaseFeature = -> Pocket028
  CheckUpToFaceLimits = true
  ClaimChildren = false
  Direction = (0,0,1)
  Fit = 0
  FitJoin = 0
  InnerFit = 0
  InnerFitJoin = 0
  InvalidShape = false
  Length = 0.4
  Length2 = 100
  Linearize = true
  NewSolid = false
  Profile = -> Sketch059
  Refine = true
  Suppress = false
  TaperInnerAngle = 0
  TaperInnerAngleRev = 0
  TreeRank = 626
  Type = 0
  ValidateShape = true
  _ProfileBasedVersion = 1
FEATURE [PartDesign::Fillet] Fillet019
  AddSubType = 0
  Base = -> Pad032 [Edge54,Edge61,Edge36,Edge43]
  BaseFeature = -> Pad032
  InvalidShape = false
  NewSolid = false
  Radius = 0.39
  Refine = true
  SupportTransform = false
  Suppress = false
  TreeRank = 627
  UseAllEdges = false
  ValidateShape = true
FEATURE [PartDesign::PolarPattern] PolarPattern006
  AddSubType = 0
  Angle = 360
  Axis = -> Z_Axis029
  BaseFeature = -> Fillet019
  CopyShape = false
  HideBaseFeature = false
  InvalidShape = false
  NewSolid = false
  Occurrences = 35
  OffsetBaseFeature = true
  OriginalSubs = -> [Fillet019,Pad032,Pocket028,Pad031,Pocket027]
  Originals = -> [Fillet019,Pad032,Pocket028,Pad031,Pocket027]
  ParallelTransform = true
  Refine = true
  SubTransform = true
  Suppress = false
  TreeRank = 628
  ValidateShape = true
  _Version = 3
FEATURE [PartDesign::Body] Body027  label="WS2812B"
  AutoGroupSolids = false
  ClaimAllChildren = false
  ExportMode = 0
  Group = -> [Sketch056,Pad031,Sketch057,Pocket027,Sketch058,Pocket028,Sketch059,Pad032,Fillet019,PolarPattern006]
  InvalidShape = false
  Origin = -> Origin053
  Placement = pos=(0,0,1.6) rot=(0,0,1;0rad)
  SingleSolid = true
  Tip = -> PolarPattern006
  TreeRank = 613
  ValidateShape = true
  _ExportChildren = -> [Pad031,Pocket027,Pocket028,Pad032,Fillet019,PolarPattern006]
  _GroupVersion = 1
FEATURE [Sketcher::SketchObject] Sketch060
  ArcFitTolerance = 1e-06
  AttachmentSupport = -> [XY_Plane028]
  ExternalBSplineMaxDegree = 0
  ExternalBSplineTolerance = 0
  ExternalGeometry = -> [Fillet018]
  FullyConstrained = true
  InternalTolerance = 1e-06
  InvalidShape = false
  MakeInternals = false
  MapMode = 5
  Support = -> [XY_Plane028]
  TreeRank = 629
  ValidateShape = true
  sketch-geometry (4):
    g0: ArcOfCircle CenterX=-2.194e-13 CenterY=-6.7607e-12 CenterZ=0 NormalX=0 NormalY=0 NormalZ=1 AngleXU=0 Radius=38.75 StartAngle=1.37192 EndAngle=1.41063
    g1: LineSegment [constr] StartX=-2.194e-13 StartY=-6.7607e-12 StartZ=0 EndX=7.14974 EndY=39.3983 EndZ=0
    g2: LineSegment StartX=6.17984 StartY=38.254 StartZ=0 EndX=7.14974 EndY=39.3983 EndZ=0
    g3: LineSegment StartX=7.14974 StartY=39.3983 StartZ=0 EndX=7.65573 EndY=37.9862 EndZ=0
  constraints (11):
    c: Coincident(g0,g-3)
    c: PointOnObject(g0,g-3)
    c: Coincident(g1,g0)
    c: Coincident(g2,g0)
    c: Coincident(g2,g1)
    c: Coincident(g3,g2)
    c: Coincident(g3,g0)
    c: Equal(g3,g2)
    c: Angle(g1,g-2) = 0.17952
    c: Distance(g0,g0) = 1.5
    c: Distance(g3) = 1.5
FEATURE [PartDesign::Pocket] Pocket029
  AddSubType = 1
  AutoTaperInnerAngle = false
  BaseFeature = -> Fillet018
  CheckUpToFaceLimits = true
  ClaimChildren = false
  Direction = (1,1,1)
  Fit = 0
  FitJoin = 0
  InnerFit = 0
  InnerFitJoin = 0
  InvalidShape = false
  Length = 5
  Length2 = 100
  Linearize = true
  NewSolid = false
  Profile = -> Sketch060
  Refine = true
  Reversed = true
  Suppress = false
  TaperInnerAngle = 0
  TaperInnerAngleRev = 0
  TreeRank = 630
  Type = 0
  ValidateShape = true
  _ProfileBasedVersion = 1
  _Version = 1
FEATURE [PartDesign::Fillet] Fillet020
  AddSubType = 0
  Base = -> Pocket029 [Edge48,Edge52]
  BaseFeature = -> Pocket029
  InvalidShape = false
  NewSolid = false
  Radius = 1
  Refine = true
  SupportTransform = false
  Suppress = false
  TreeRank = 631
  UseAllEdges = false
  ValidateShape = true
FEATURE [PartDesign::Body] Body026  label="PCBRingLed"
  AutoGroupSolids = false
  ClaimAllChildren = false
  ExportMode = 0
  Group = -> [Sketch054,Pad029,Sketch055,Pad030,Fillet018,Sketch060,Pocket029,Fillet020]
  InvalidShape = false
  Origin = -> Origin052
  SingleSolid = true
  Tip = -> Fillet020
  TreeRank = 603
  ValidateShape = true
  _ExportChildren = -> [Pad029,Pad030,Fillet018,Pocket029,Fillet020]
  _GroupVersion = 1
FEATURE [App::Part] Part006  label="Ring35Leds"
  ClaimAllChildren = false
  ExportMode = 1
  Group = -> [Body026,Body027]
  Origin = -> Origin051
  Placement = pos=(-1.32e-14,1.77e-14,59) rot=(0,0,-1;1.91488rad)
  TreeRank = 593
  _ExportChildren = -> [Body026,Body027]
  _GroupVersion = 1
FEATURE [Part::SubShapeBinder] Import004  label="Import004(Fillet020)"
  BindCopyOnChange = 0
  BindMode = 0
  ClaimChildren = false
  Context = -> <external ../table_2022.FCStd>#Group [Link005.Group002.Link014.Group004.Body023.Import004.]
  EdgeTolerance = 1e-06
  FillStyle = 0
  Fuse = false
  InvalidShape = false
  MakeFace = false
  MergeEdges = true
  OffsetFill = false
  OffsetIntersection = false
  OffsetJoinType = 0
  OffsetOpenResult = false
  Outline = false
  PartialLoad = false
  Relative = true
  SplitEdges = false
  Support = -> [Part006[Body026.Fillet020.]]
  TightBound = false
  TreeRank = 633
  ValidateShape = true
  _Version = 8
FEATURE [Part::SubShapeBinder] Import005  label="Import005(Pocket077)"
  BindCopyOnChange = 0
  BindMode = 0
  ClaimChildren = false
  Context = -> Part007 [Body028.Import005.]
  EdgeTolerance = 1e-06
  FillStyle = 0
  Fuse = false
  InvalidShape = false
  MakeFace = false
  MergeEdges = true
  OffsetFill = false
  OffsetIntersection = false
  OffsetJoinType = 0
  OffsetOpenResult = false
  Outline = false
  PartialLoad = false
  Relative = true
  SplitEdges = false
  Support = -> [Link001[Body090.Pocket077.Face32]]
  TightBound = false
  TreeRank = 655
  ValidateShape = true
  _Version = 8
FEATURE [Part::FeaturePython] Screw  label="M3x10-Screw"  # WARN: FeaturePython — macro-defined, semantics opaque (R4)
  BaseObject = -> Body028 [Edge60]
  Diameter = 1
  InvalidShape = false
  Invert = false
  LeftHanded = false
  Length = 2
  LengthCustom = 10
  MatchOuter = false
  OffsetAngle = 0
  Placement = pos=(-25.9808,15,51.3) rot=(0,0,1;0rad)
  Thread = false
  TreeRank = 659
  Type = 84
  ValidateShape = true
FEATURE [Part::FeaturePython] Screw001  label="M3x10-Screw001"  # WARN: FeaturePython — macro-defined, semantics opaque (R4)
  BaseObject = -> Body028 [Edge53]
  Diameter = 1
  InvalidShape = false
  Invert = false
  LeftHanded = false
  Length = 2
  LengthCustom = 10
  MatchOuter = false
  OffsetAngle = 0
  Placement = pos=(15,25.9808,51.3) rot=(0,0,1;0rad)
  Thread = false
  TreeRank = 660
  Type = 84
  ValidateShape = true
FEATURE [App::DocumentObjectGroup] Group006  label="Visserie"
  ClaimAllChildren = true
  ExportMode = 1
  Group = -> [Screw,Screw001,PcbStandoff,PcbStandoff001,PcbStandoff002]
  TreeRank = 661
  _GroupVersion = 1
FEATURE [PartDesign::SubShapeBinder] Binder  label="Binder(Fillet021)"
  BindCopyOnChange = 0
  BindMode = 0
  ClaimChildren = false
  Context = -> <external ../robot_holonome.FCStd>#Part [Group002.Link014.Group004.Body.Binder.]
  EdgeTolerance = 1e-06
  FillStyle = 0
  Fuse = false
  InvalidShape = false
  MakeFace = true
  MergeEdges = true
  OffsetFill = false
  OffsetIntersection = false
  OffsetJoinType = 0
  OffsetOpenResult = false
  Outline = false
  PartialLoad = false
  Relative = true
  SplitEdges = false
  Support = -> [Body023[Fillet021.Face140]]
  TightBound = false
  TreeRank = 679
  ValidateShape = true
  _Version = 8
FEATURE [Sketcher::SketchObject] Sketch066
  ArcFitTolerance = 1e-06
  AttachmentSupport = -> [Binder]
  ExternalBSplineMaxDegree = 0
  ExternalBSplineTolerance = 0
  ExternalGeometry = -> [Binder]
  FullyConstrained = true
  InternalTolerance = 1e-06
  InvalidShape = false
  MakeInternals = false
  MapMode = 5
  Placement = pos=(0,0,3) rot=(1,0,0;3.14159rad)
  Support = -> [Binder]
  TreeRank = 680
  ValidateShape = true
  sketch-geometry (3):
    g0: Circle CenterX=-24.3484 CenterY=30.5 CenterZ=0 NormalX=0 NormalY=0 NormalZ=1 AngleXU=0 Radius=1.6
    g1: Circle CenterX=38.588 CenterY=5.83631 CenterZ=0 NormalX=0 NormalY=0 NormalZ=1 AngleXU=0 Radius=1.6
    g2: Circle CenterX=-14.2396 CenterY=-36.3363 CenterZ=0 NormalX=0 NormalY=0 NormalZ=1 AngleXU=0 Radius=1.6
  constraints (6):
    c: Coincident(g0,g-3)
    c: Coincident(g1,g-5)
    c: Coincident(g2,g-4)
    c: Equal(g2,g1)
    c: Equal(g2,g0)
    c: Diameter(g2) = 3.2
FEATURE [PartDesign::Pocket] Pocket032
  AddSubType = 1
  AutoTaperInnerAngle = false
  BaseFeature = -> Fillet
  CheckUpToFaceLimits = true
  ClaimChildren = false
  Direction = (0,0,1)
  Fit = 0
  FitJoin = 0
  InnerFit = 0
  InnerFitJoin = 0
  InvalidShape = false
  Length = 5
  Length2 = 100
  Linearize = true
  NewSolid = false
  Profile = -> Sketch066
  Refine = true
  Reversed = true
  Suppress = false
  TaperInnerAngle = 0
  TaperInnerAngleRev = 0
  TreeRank = 681
  Type = 1
  ValidateShape = true
  _ProfileBasedVersion = 1
  _Version = 1
FEATURE [Sketcher::SketchObject] Sketch067
  ArcFitTolerance = 1e-06
  AttachmentSupport = -> [XY_Plane031]
  ExternalBSplineMaxDegree = 0
  ExternalBSplineTolerance = 0
  FullyConstrained = true
  InternalTolerance = 1e-06
  InvalidShape = false
  MakeInternals = false
  MapMode = 5
  Support = -> [XY_Plane031]
  TreeRank = 692
  ValidateShape = true
  sketch-geometry (7):
    g0: Circle CenterX=-2.1495e-12 CenterY=1.07369e-11 CenterZ=0 NormalX=0 NormalY=0 NormalZ=1 AngleXU=0 Radius=49.5
    g1: Circle CenterX=-1.1313e-12 CenterY=33 CenterZ=0 NormalX=0 NormalY=0 NormalZ=1 AngleXU=0 Radius=1.6
    g2: Circle CenterX=-28.5788 CenterY=-16.5 CenterZ=0 NormalX=0 NormalY=0 NormalZ=1 AngleXU=0 Radius=1.6
    g3: Circle CenterX=28.5788 CenterY=-16.5 CenterZ=0 NormalX=0 NormalY=0 NormalZ=1 AngleXU=0 Radius=1.6
    g4: LineSegment [constr] StartX=-28.5788 StartY=-16.5 StartZ=0 EndX=-2.1494e-12 EndY=1.07363e-11 EndZ=0
    g5: LineSegment [constr] StartX=-2.1495e-12 StartY=1.07369e-11 StartZ=0 EndX=-1.1313e-12 EndY=33 EndZ=0
    g6: LineSegment [constr] StartX=-2.1495e-12 StartY=1.07369e-11 StartZ=0 EndX=28.5788 EndY=-16.5 EndZ=0
  constraints (17):
    c: Coincident(g0,g-1)
    c: Diameter(g0) = 99
    c: PointOnObject(g1,g-2)
    c: Coincident(g4,g2)
    c: Coincident(g4,g0)
    c: Coincident(g5,g0)
    c: Coincident(g5,g1)
    c: Coincident(g6,g0)
    c: Coincident(g6,g3)
    c: Equal(g6,g4)
    c: Equal(g4,g5)
    c: Angle(g6,g5) = 2.0944
    c: Angle(g5,g4) = 2.0944
    c: DistanceY(g5,g5) = 33
    c: Equal(g3,g1)
    c: Equal(g3,g2)
    c: Diameter(g3) = 3.2
FEATURE [PartDesign::Pad] Pad034
  AddSubType = 0
  AlongSketchNormal = false
  AutoTaperInnerAngle = false
  CheckUpToFaceLimits = true
  ClaimChildren = false
  Direction = (0,0,1)
  Fit = 0
  FitJoin = 0
  InnerFit = 0
  InnerFitJoin = 0
  InvalidShape = false
  Length = 3
  Length2 = 100
  Linearize = true
  NewSolid = false
  Profile = -> Sketch067
  Refine = true
  Suppress = false
  TaperInnerAngle = 0
  TaperInnerAngleRev = 0
  TreeRank = 693
  Type = 0
  ValidateShape = true
  _ProfileBasedVersion = 1
FEATURE [PartDesign::Body] Body029  label="TopSupport"
  AutoGroupSolids = false
  ClaimAllChildren = false
  ExportMode = 0
  Group = -> [Sketch067,Pad034]
  InvalidShape = false
  Origin = -> Origin055
  Placement = pos=(0,0,92) rot=(0,0,1;0rad)
  SingleSolid = true
  Tip = -> Pad034
  TreeRank = 691
  ValidateShape = true
  _ExportChildren = -> [Pad034]
  _GroupVersion = 1
FEATURE [Sketcher::SketchObject] Sketch069
  ArcFitTolerance = 1e-06
  AttachmentSupport = -> [XY_Plane033]
  ExternalBSplineMaxDegree = 0
  ExternalBSplineTolerance = 0
  FullyConstrained = true
  InternalTolerance = 1e-06
  InvalidShape = false
  MakeInternals = false
  MapMode = 5
  Support = -> [XY_Plane033]
  TreeRank = 717
  ValidateShape = true
  sketch-geometry (1):
    g0: Circle CenterX=0 CenterY=0 CenterZ=0 NormalX=0 NormalY=0 NormalZ=1 AngleXU=0 Radius=48.5
  constraints (2):
    c: Coincident(g0,g-1)
    c: Diameter(g0) = 97
FEATURE [PartDesign::Pad] Pad036
  AddSubType = 0
  AlongSketchNormal = false
  AutoTaperInnerAngle = false
  CheckUpToFaceLimits = true
  ClaimChildren = false
  Direction = (0,0,1)
  Fit = 0
  FitJoin = 0
  InnerFit = 0
  InnerFitJoin = 0
  InvalidShape = false
  Length = 2
  Length2 = 100
  Linearize = true
  NewSolid = false
  Profile = -> Sketch069
  Refine = true
  Suppress = false
  TaperInnerAngle = 0
  TaperInnerAngleRev = 0
  TreeRank = 718
  Type = 0
  ValidateShape = true
  _ProfileBasedVersion = 1
FEATURE [PartDesign::Fillet] Fillet024
  AddSubType = 0
  Base = -> Pad036 [Edge3]
  BaseFeature = -> Pad036
  InvalidShape = false
  NewSolid = false
  Radius = 1.9
  Refine = true
  SupportTransform = false
  Suppress = false
  TreeRank = 719
  UseAllEdges = false
  ValidateShape = true
FEATURE [PartDesign::Body] Body031  label="SupportCrochet"
  AutoGroupSolids = false
  ClaimAllChildren = false
  ExportMode = 0
  Group = -> [Sketch069,Pad036,Fillet024]
  InvalidShape = false
  Origin = -> Origin057
  Placement = pos=(0,0,95) rot=(0,0,1;0rad)
  SingleSolid = true
  Tip = -> Fillet024
  TreeRank = 716
  ValidateShape = true
  _ExportChildren = -> [Pad036,Fillet024]
  _GroupVersion = 1
FEATURE [PartDesign::SubShapeBinder] Binder006  label="Binder006(Pad034)"
  BindCopyOnChange = 0
  BindMode = 0
  ClaimChildren = false
  Context = -> <external ../robot_holonome.FCStd>#Part [Group002.Link014.Body033.Binder006.]
  EdgeTolerance = 1e-06
  FillStyle = 0
  FixShape = 1
  Fuse = false
  InvalidShape = false
  MakeFace = true
  MergeEdges = true
  OffsetFill = false
  OffsetIntersection = false
  OffsetJoinType = 0
  OffsetOpenResult = false
  Outline = false
  PartialLoad = false
  Relative = true
  SplitEdges = false
  Support = -> [Body029[Pad034.Face5]]
  TightBound = false
  TreeRank = 794
  ValidateShape = false
  _Version = 8
FEATURE [Sketcher::SketchObject] Sketch075
  ArcFitTolerance = 1e-06
  AttachmentSupport = -> [XY_Plane035]
  ExternalBSplineMaxDegree = 5
  ExternalBSplineTolerance = 0.0001
  ExternalGeometry = -> [Binder006]
  FixShape = 1
  FullyConstrained = true
  InternalTolerance = 1e-06
  InvalidShape = false
  MakeInternals = false
  MapMode = 5
  Support = -> [XY_Plane035]
  TreeRank = 795
  ValidateShape = false
FEATURE [PartDesign::Pad] Pad039
  AddSubType = 0
  AlongSketchNormal = false
  AutoTaperInnerAngle = true
  CheckUpToFaceLimits = true
  ClaimChildren = false
  Direction = (0,0,1)
  Fit = 0
  FitJoin = 0
  FixShape = 1
  InnerFit = 0
  InnerFitJoin = 0
  InvalidShape = false
  Length = 7.5
  Length2 = 10
  Linearize = true
  NewSolid = false
  Profile = -> Sketch075
  ReferenceAxis = -> Sketch075 [N_Axis]
  Refine = true
  Reversed = true
  Suppress = false
  TaperInnerAngle = 0
  TaperInnerAngleRev = 0
  TreeRank = 796
  Type = 0
  ValidateShape = true
  _ProfileBasedVersion = 1
FEATURE [Sketcher::SketchObject] Sketch076
  ArcFitTolerance = 1e-06
  AttachmentSupport = -> [Pad039]
  ExternalBSplineMaxDegree = 5
  ExternalBSplineTolerance = 0.0001
  ExternalGeometry = -> [Pad039]
  FixShape = 1
  FullyConstrained = true
  InternalTolerance = 1e-06
  InvalidShape = false
  MakeInternals = false
  MapMode = 5
  Placement = pos=(0,0,-7.5) rot=(1,0,0;3.14159rad)
  Support = -> [Pad039]
  TreeRank = 797
  ValidateShape = false
  sketch-geometry (4):
    g0: Circle CenterX=0 CenterY=0 CenterZ=0 NormalX=0 NormalY=0 NormalZ=1 AngleXU=0 Radius=19
    g1: Circle CenterX=28.5788 CenterY=16.5 CenterZ=0 NormalX=0 NormalY=0 NormalZ=1 AngleXU=0 Radius=6
    g2: Circle CenterX=-28.5788 CenterY=16.5 CenterZ=0 NormalX=0 NormalY=0 NormalZ=1 AngleXU=0 Radius=6
    g3: Circle CenterX=0 CenterY=-33 CenterZ=0 NormalX=0 NormalY=0 NormalZ=1 AngleXU=0 Radius=6
  constraints (8):
    c: Coincident(g0,g-1)
    c: Diameter(g0) = 38
    c: Coincident(g1,g-3)
    c: Coincident(g2,g-4)
    c: Coincident(g3,g-5)
    c: Equal(g3,g1)
    c: Equal(g3,g2)
    c: Diameter(g3) = 12
FEATURE [PartDesign::Pocket] Pocket036
  AddSubType = 1
  AlongSketchNormal = false
  AutoTaperInnerAngle = true
  BaseFeature = -> Pad039
  CheckUpToFaceLimits = true
  ClaimChildren = false
  Direction = (0,0,1)
  Fit = 0
  FitJoin = 0
  FixShape = 1
  InnerFit = 0
  InnerFitJoin = 0
  InvalidShape = false
  Length = 2.5
  Length2 = 10
  Linearize = true
  NewSolid = false
  Profile = -> Sketch076
  ReferenceAxis = -> Sketch076 [N_Axis]
  Refine = true
  Suppress = false
  TaperInnerAngle = 0
  TaperInnerAngleRev = 0
  TreeRank = 798
  Type = 0
  ValidateShape = true
  _ProfileBasedVersion = 1
  _Version = 1
FEATURE [PartDesign::Chamfer] Chamfer012
  AddSubType = 0
  Angle = 45
  Base = -> Pocket036 [Edge8,Edge9,Edge7,Edge10,Edge3]
  BaseFeature = -> Pocket036
  ChamferType = 0
  FixShape = 1
  FlipDirection = false
  InvalidShape = false
  NewSolid = false
  Refine = true
  Size = 1
  Size2 = 1
  SupportTransform = false
  Suppress = false
  TreeRank = 799
  UseAllEdges = false
  ValidateShape = true
FEATURE [PartDesign::Chamfer] Chamfer013
  AddSubType = 0
  Angle = 45
  Base = -> Chamfer012 [Edge16,Edge18,Edge8,Edge7,Edge14,Edge6,Edge3]
  BaseFeature = -> Chamfer012
  ChamferType = 0
  FixShape = 1
  FlipDirection = false
  InvalidShape = false
  NewSolid = false
  Refine = true
  Size = 0.4
  Size2 = 1
  SupportTransform = false
  Suppress = false
  TreeRank = 800
  UseAllEdges = false
  ValidateShape = true
FEATURE [PartDesign::Body] Body033  label="CasquetteTop"
  AutoGroupSolids = false
  ClaimAllChildren = false
  ExportMode = 0
  FixShape = 1
  Group = -> [Binder006,Sketch075,Pad039,Sketch076,Pocket036,Chamfer012,Chamfer013]
  InvalidShape = false
  Origin = -> Origin059
  Placement = pos=(0,0,92) rot=(0,0,1;0rad)
  SingleSolid = true
  Tip = -> Chamfer013
  TreeRank = 793
  ValidateShape = false
  _ExportChildren = -> [Binder006,Pad039,Pocket036,Chamfer012,Chamfer013]
  _GroupVersion = 1
FEATURE [PartDesign::SubShapeBinder] Binder007  label="Binder007(Fillet011)"
  BindCopyOnChange = 0
  BindMode = 0
  ClaimChildren = false
  Context = -> <external ../robot_holonome.FCStd>#Part [Group002.Link014.Body034.Binder007.]
  EdgeTolerance = 1e-06
  FillStyle = 0
  FixShape = 1
  Fuse = false
  InvalidShape = false
  MakeFace = true
  MergeEdges = true
  OffsetFill = false
  OffsetIntersection = false
  OffsetJoinType = 0
  OffsetOpenResult = false
  Outline = false
  PartialLoad = false
  Relative = true
  SplitEdges = false
  Support = -> [Body024[Fillet011.Face5]]
  TightBound = false
  TreeRank = 811
  ValidateShape = false
  _Version = 8
FEATURE [PartDesign::Pad] Pad040
  AddSubType = 0
  AlongSketchNormal = false
  AutoTaperInnerAngle = true
  CheckUpToFaceLimits = true
  ClaimChildren = false
  Direction = (0,0,1)
  Fit = 0
  FitJoin = 0
  FixShape = 1
  InnerFit = 0
  InnerFitJoin = 0
  InvalidShape = false
  Length = 5
  Length2 = 10
  Linearize = true
  NewSolid = false
  Profile = -> Binder007
  Refine = true
  Suppress = false
  TaperInnerAngle = 0
  TaperInnerAngleRev = 0
  TreeRank = 812
  Type = 0
  ValidateShape = true
  _ProfileBasedVersion = 1
FEATURE [Sketcher::SketchObject] Sketch077
  ArcFitTolerance = 1e-06
  AttachmentSupport = -> [XY_Plane036]
  ExternalBSplineMaxDegree = 5
  ExternalBSplineTolerance = 0.0001
  ExternalGeometry = -> [Pad040]
  FixShape = 1
  FullyConstrained = true
  InternalTolerance = 1e-06
  InvalidShape = false
  MakeInternals = false
  MapMode = 5
  Support = -> [XY_Plane036]
  TreeRank = 813
  ValidateShape = false
  sketch-geometry (3):
    g0: Circle CenterX=0 CenterY=33 CenterZ=0 NormalX=0 NormalY=0 NormalZ=1 AngleXU=0 Radius=4
    g1: Circle CenterX=28.5788 CenterY=-16.5 CenterZ=0 NormalX=0 NormalY=0 NormalZ=1 AngleXU=0 Radius=4
    g2: Circle CenterX=-28.5788 CenterY=-16.5 CenterZ=0 NormalX=0 NormalY=0 NormalZ=1 AngleXU=0 Radius=4
  constraints (6):
    c: Coincident(g0,g-3)
    c: Coincident(g1,g-4)
    c: Coincident(g2,g-5)
    c: Equal(g0,g1)
    c: Equal(g0,g2)
    c: Diameter(g0) = 8
FEATURE [PartDesign::Pocket] Pocket037
  AddSubType = 1
  AlongSketchNormal = false
  AutoTaperInnerAngle = true
  BaseFeature = -> Pad040
  CheckUpToFaceLimits = true
  ClaimChildren = false
  Direction = (0,0,-1)
  Fit = 0
  FitJoin = 0
  FixShape = 1
  InnerFit = 0
  InnerFitJoin = 0
  InvalidShape = false
  Length = 5
  Length2 = 10
  Linearize = true
  NewSolid = false
  Profile = -> Sketch077
  ReferenceAxis = -> Sketch077 [N_Axis]
  Refine = true
  Reversed = true
  Suppress = false
  TaperInnerAngle = 0
  TaperInnerAngleRev = 0
  TreeRank = 814
  Type = 1
  ValidateShape = true
  _ProfileBasedVersion = 1
  _Version = 1
FEATURE [PartDesign::Chamfer] Chamfer014
  AddSubType = 0
  Angle = 45
  Base = -> Pocket037 [Edge20]
  BaseFeature = -> Pocket037
  ChamferType = 1
  FixShape = 1
  FlipDirection = false
  InvalidShape = false
  NewSolid = false
  Refine = true
  Size = 8
  Size2 = 3
  SupportTransform = false
  Suppress = false
  TreeRank = 815
  UseAllEdges = false
  ValidateShape = true
FEATURE [PartDesign::Chamfer] Chamfer015
  AddSubType = 0
  Angle = 45
  Base = -> Chamfer014 [Edge6,Edge12,Edge3,Edge2,Edge17,Edge35,Edge15,Edge38,Edge25]
  BaseFeature = -> Chamfer014
  ChamferType = 0
  FixShape = 1
  FlipDirection = false
  InvalidShape = false
  NewSolid = false
  Refine = true
  Size = 0.6
  Size2 = 1
  SupportTransform = false
  Suppress = false
  TreeRank = 816
  UseAllEdges = false
  ValidateShape = true
FEATURE [PartDesign::Body] Body034  label="Cache"
  AutoGroupSolids = false
  ClaimAllChildren = false
  ExportMode = 0
  FixShape = 1
  Group = -> [Binder007,Pad040,Sketch077,Pocket037,Chamfer014,Chamfer015]
  InvalidShape = false
  Origin = -> Origin060
  Placement = pos=(0,0,67) rot=(0,0,1;0rad)
  SingleSolid = true
  Tip = -> Chamfer015
  TreeRank = 810
  ValidateShape = false
  _ExportChildren = -> [Pad040,Pocket037,Chamfer014,Chamfer015]
  _GroupVersion = 1
FEATURE [Sketcher::SketchObject] Sketch078
  ArcFitTolerance = 1e-06
  AttachmentSupport = -> [Pocket032]
  ExternalBSplineMaxDegree = 5
  ExternalBSplineTolerance = 0.0001
  ExternalGeometry = -> [Pocket032]
  FullyConstrained = true
  InternalTolerance = 1e-06
  InvalidShape = false
  MakeInternals = false
  MapMode = 5
  Placement = pos=(0,0,3) rot=(0,0,1;0rad)
  Support = -> [Pocket032]
  TreeRank = 820
  ValidateShape = false
  sketch-geometry (6):
    g0: ArcOfCircle [constr] CenterX=25 CenterY=45 CenterZ=0 NormalX=0 NormalY=0 NormalZ=1 AngleXU=0 Radius=3 StartAngle=1.91805 EndAngle=4.36514
    g1: ArcOfCircle [constr] CenterX=31.8096 CenterY=45 CenterZ=0 NormalX=0 NormalY=0 NormalZ=1 AngleXU=0 Radius=5.31738 StartAngle=4.36514 EndAngle=8.20123
    g2: LineSegment [constr] StartX=23.9791 StartY=42.1791 StartZ=0 EndX=30 EndY=40 EndZ=0
    g3: LineSegment [constr] StartX=30 StartY=50 StartZ=0 EndX=23.9791 EndY=47.8209 EndZ=0
    g4: LineSegment [constr] StartX=30 StartY=50 StartZ=0 EndX=30 EndY=40 EndZ=0
    g5: Circle CenterX=25 CenterY=45 CenterZ=0 NormalX=0 NormalY=0 NormalZ=1 AngleXU=0 Radius=3
  constraints (12):
    c: Tangent(g0,g2) = -1.5708
    c: Tangent(g2,g1) = -1.5708
    c: Tangent(g1,g3) = -1.5708
    c: Tangent(g3,g0) = -1.5708
    c: Coincident(g0,g-3)
    c: Coincident(g4,g3)
    c: Coincident(g4,g2)
    c: DistanceY(g4,g4) = 10
    c: Radius(g0) = 3
    c: Coincident(g2,g-4)
    c: Coincident(g5,g-3)
    c: PointOnObject(g0,g5)
FEATURE [PartDesign::Pocket] Pocket038
  AddSubType = 1
  AlongSketchNormal = false
  AutoTaperInnerAngle = true
  BaseFeature = -> Pocket032
  CheckUpToFaceLimits = true
  ClaimChildren = false
  Direction = (0,0,-1)
  Fit = 0
  FitJoin = 0
  InnerFit = 0
  InnerFitJoin = 0
  InvalidShape = false
  Length = 5
  Length2 = 10
  Linearize = true
  NewSolid = false
  Profile = -> Sketch078
  ReferenceAxis = -> Sketch078 [N_Axis]
  Refine = true
  Suppress = false
  TaperInnerAngle = 0
  TaperInnerAngleRev = 0
  TreeRank = 821
  Type = 0
  ValidateShape = true
  _ProfileBasedVersion = 1
  _Version = 1
FEATURE [PartDesign::PolarPattern] PolarPattern007
  AddSubType = 0
  Angle = 360
  Axis = -> Sketch078 [N_Axis]
  BaseFeature = -> Pocket038
  CopyShape = false
  HideBaseFeature = false
  InvalidShape = false
  NewSolid = false
  Occurrences = 3
  OffsetBaseFeature = true
  OriginalSubs = -> [Pocket038]
  Originals = -> [Pocket038]
  ParallelTransform = true
  Refine = true
  SubTransform = true
  Suppress = false
  TreeRank = 822
  ValidateShape = true
  _Version = 3
FEATURE [PartDesign::Chamfer] Chamfer017
  AddSubType = 0
  Angle = 45
  Base = -> PolarPattern007 [Edge62,Edge60,Edge57,Edge94,Edge91,Edge64,Edge66,Edge87,Edge53,Edge69,Edge55,Edge89]
  BaseFeature = -> PolarPattern007
  ChamferType = 0
  FlipDirection = false
  InvalidShape = false
  NewSolid = false
  Refine = true
  Size = 3
  Size2 = 1
  SupportTransform = false
  Suppress = false
  TreeRank = 824
  UseAllEdges = false
  ValidateShape = true
FEATURE [PartDesign::Body] Body  label="SupportBeacon"
  AutoGroupSolids = false
  ClaimAllChildren = false
  ExportMode = 0
  Group = -> [Sketch,Pad,Sketch001,PolarPattern,Pocket,PolarPattern001,Chamfer,Fillet,Binder,Sketch066,Pocket032,Sketch078,Pocket038,PolarPattern007,Chamfer017]
  InvalidShape = false
  Origin = -> Origin
  SingleSolid = true
  Tip = -> Chamfer017
  TreeRank = 0
  ValidateShape = true
  _ExportChildren = -> [Pad,PolarPattern,Pocket,PolarPattern001,Chamfer,Fillet,Binder,Pocket032,Pocket038,PolarPattern007,Chamfer017]
  _GroupVersion = 1
FEATURE [TechDraw::DrawSVGTemplate] Template
  Height = 210
  Orientation = 1
  Template = <path>
  TreeRank = 828
  Width = 297
FEATURE [TechDraw::DrawProjGroupItem] ProjItem  label="Front"
  CoarseView = false
  Direction = (0,0,1)
  Focus = 100
  HardHidden = false
  IsoCount = 0
  IsoHidden = false
  IsoVisible = false
  LockPosition = true
  Perspective = false
  Rotation = 0
  RotationVector = (1,0,0)
  ScaleType = 2
  ScrubCount = 0
  SeamHidden = false
  SeamVisible = true
  SmoothHidden = false
  SmoothVisible = true
  Source = -> [Chamfer017]
  TreeRank = 831
  Type = 0
  X = 0
  XDirection = (1,0,0)
  Y = 0
FEATURE [TechDraw::DrawProjGroup] ProjGroup
  Anchor = -> ProjItem
  AutoDistribute = true
  LockPosition = false
  ProjectionType = 0
  Rotation = 0
  ScaleType = 0
  Source = -> [Chamfer017]
  TreeRank = 832
  Views = -> [ProjItem]
  X = 70.2686
  Y = 146.599
  spacingX = 15
  spacingY = 15
FEATURE [TechDraw::DrawPage] Page  label="Laser3mm-SupportBeacon"
  KeepUpdated = true
  NextBalloonIndex = 1
  ProjectionType = 0
  Template = -> Template
  TreeRank = 829
  Views = -> [ProjGroup]
FEATURE [PartDesign::Body] Body023  label="CoqueLidar"
  AutoGroupSolids = false
  ClaimAllChildren = false
  ExportMode = 0
  Group = -> [Sketches,Datums,Misc,Sketch042,Pad026,Sketch043,Revolution004,Sketch044,Pocket019,Sketch045,Pocket020,Sketch047,Pocket021,Fillet012,Sketch048,Export004,Export005,Pocket022,Pocket023,Sketch049,Sketch050,Pocket024,Sketch051,Pocket025,Fillet013,Fillet014,Fillet015,Sketch052,Pocket026,Fillet016,Chamfer002,Chamfer003,Chamfer004,Chamfer005,Chamfer006,Chamfer007,Chamfer008,Sketch061,Import004,Sketch062,+7 more]
  InvalidShape = true
  Origin = -> Origin031
  Placement = pos=(0,0,3) rot=(0,0,1;0rad)
  SingleSolid = true
  Tip = -> Pad041
  TreeRank = 401
  ValidateShape = true
  _ExportChildren = -> [Sketches,Datums,Misc,Pad026,Revolution004,Pocket019,Pocket020,Pocket021,Fillet012,Pocket022,Pocket023,Pocket024,Pocket025,Fillet013,Fillet014,Fillet015,Pocket026,Fillet016,Chamfer002,Chamfer003,Chamfer004,Chamfer005,Chamfer006,Chamfer007,Chamfer008,Loft,Pocket030,Fillet021,Pad041]
  _GroupVersion = 1
FEATURE [Sketcher::SketchObject] Sketch048
  ArcFitTolerance = 0
  AttachmentSupport = -> [Fillet012]
  Exports = -> [Export004,Export005]
  ExternalBSplineMaxDegree = 0
  ExternalBSplineTolerance = 0
  ExternalGeometry = -> [Fillet012]
  FullyConstrained = true
  InternalTolerance = 1e-06
  InvalidShape = false
  MakeInternals = false
  MapMode = 5
  Placement = pos=(-1e-14,1.31e-14,45.3) rot=(0,0,1;0rad)
  Support = -> [Fillet012]
  TreeRank = 428
  ValidateShape = true
  sketch-geometry (14):
    g0: ArcOfCircle CenterX=9.947e-12 CenterY=33 CenterZ=0 NormalX=0 NormalY=0 NormalZ=1 AngleXU=0 Radius=5 StartAngle=3.84718 EndAngle=5.57759
    g1: ArcOfCircle CenterX=28.5788 CenterY=-16.5 CenterZ=0 NormalX=0 NormalY=0 NormalZ=1 AngleXU=0 Radius=5 StartAngle=1.75279 EndAngle=3.4832
    g2: ArcOfCircle CenterX=-28.5788 CenterY=-16.5 CenterZ=0 NormalX=0 NormalY=0 NormalZ=1 AngleXU=0 Radius=5 StartAngle=5.94158 EndAngle=7.67199
    g3: ArcOfCircle CenterX=-1.6183e-11 CenterY=2.7227e-12 CenterZ=0 NormalX=0 NormalY=0 NormalZ=1 AngleXU=0 Radius=30 StartAngle=1.69801 EndAngle=2.48456
    g4: ArcOfCircle CenterX=-1.6183e-11 CenterY=2.7227e-12 CenterZ=0 NormalX=0 NormalY=0 NormalZ=1 AngleXU=0 Radius=30 StartAngle=5.8868 EndAngle=7.19695
    g5: ArcOfCircle CenterX=-1.6183e-11 CenterY=2.7227e-12 CenterZ=0 NormalX=0 NormalY=0 NormalZ=1 AngleXU=0 Radius=30 StartAngle=3.79241 EndAngle=5.63237
    g6: ArcOfCircle CenterX=15 CenterY=25.9808 CenterZ=0 NormalX=0 NormalY=0 NormalZ=1 AngleXU=0 Radius=4 StartAngle=2.68471 EndAngle=5.69287
    g7: ArcOfCircle CenterX=-25.9808 CenterY=15 CenterZ=0 NormalX=0 NormalY=0 NormalZ=1 AngleXU=0 Radius=4 StartAngle=4.25551 EndAngle=7.26367
    g8: LineSegment [constr] StartX=-1.6183e-11 StartY=2.7227e-12 StartZ=0 EndX=15 EndY=25.9808 EndZ=0
    g9: LineSegment [constr] StartX=-1.6183e-11 StartY=2.7227e-12 StartZ=0 EndX=-25.9808 EndY=15 EndZ=0
    g10: ArcOfCircle CenterX=-1.6183e-11 CenterY=2.7227e-12 CenterZ=0 NormalX=0 NormalY=0 NormalZ=1 AngleXU=0 Radius=30 StartAngle=1.18063 EndAngle=1.44358
    g11: ArcOfCircle CenterX=-1.6183e-11 CenterY=2.7227e-12 CenterZ=0 NormalX=0 NormalY=0 NormalZ=1 AngleXU=0 Radius=30 StartAngle=2.75143 EndAngle=3.53798
    g12: Circle CenterX=15 CenterY=25.9808 CenterZ=0 NormalX=0 NormalY=0 NormalZ=1 AngleXU=0 Radius=2.1
    g13: Circle CenterX=-25.9808 CenterY=15 CenterZ=0 NormalX=0 NormalY=0 NormalZ=1 AngleXU=0 Radius=2.1
  constraints (41):
    c: Coincident(g0,g-3)
    c: Coincident(g1,g-5)
    c: Coincident(g2,g-4)
    c: Coincident(g3,g-1)
    c: Coincident(g11,g2)
    c: Coincident(g3,g0)
    c: Coincident(g4,g3)
    c: Coincident(g10,g0)
    c: Coincident(g4,g1)
    c: Coincident(g5,g3)
    c: Coincident(g5,g2)
    c: Coincident(g5,g1)
    c: Equal(g0,g2)
    c: Equal(g2,g1)
    c: Equal(g3,g4)
    c: Equal(g4,g5)
    c: Radius(g4) = 30
    c: PointOnObject(g0,g-3)
    c: PointOnObject(g6,g4)
    c: PointOnObject(g7,g3)
    c: PointOnObject(g7,g3)
    c: Equal(g7,g6)
    c: Coincident(g8,g3)
    c: Coincident(g8,g6)
    c: Coincident(g9,g3)
    c: Coincident(g9,g7)
    c: Perpendicular(g9,g8)
    c: Angle(g-2,g9) = 1.0472
    c: Equal(g4,g10)
    c: Coincident(g10,g6)
    c: Coincident(g4,g10)
    c: Coincident(g4,g6)
    c: Equal(g3,g11)
    c: Coincident(g3,g7)
    c: Coincident(g3,g11)
    c: PointOnObject(g11,g7)
    c: Coincident(g12,g6)
    c: Diameter(g12) = 4.2
    c: Coincident(g13,g7)
    c: Equal(g13,g12)
    c: Radius(g7) = 4
FEATURE [Sketcher::SketchExport] Export004
  Base = -> Sketch048
  BaseRefs = -> Sketch048 [edge13,edge14]
  InvalidShape = false
  Placement = pos=(-9.9e-15,1.3e-14,45.3) rot=(0,0,1;0rad)
  Refs = ;g19.edge13 | ;g20.edge14
  SyncPlacement = true
  TreeRank = 429
  ValidateShape = true
FEATURE [Sketcher::SketchExport] Export005
  Base = -> Sketch048
  BaseRefs = -> Sketch048 [edge8,edge12,edge3,edge6,edge2,edge5,edge7,edge11,edge1,edge4]
  InvalidShape = false
  Placement = pos=(-9.9e-15,1.3e-14,45.3) rot=(0,0,1;0rad)
  Refs = ;g14.edge8 | ;g18.edge12 | ;g6.edge3 | ;g9.edge6 | ;g5.edge2 | ;g8.edge5 | ;g13.edge7 | ;g17.edge11 | ;g4.edge1 | ;g7.edge4
  SyncPlacement = true
  TreeRank = 430
  ValidateShape = true
FEATURE [PartDesign::Pocket] Pocket022
  AddSubType = 1
  AutoTaperInnerAngle = false
  BaseFeature = -> Fillet012
  CheckUpToFaceLimits = true
  ClaimChildren = false
  Direction = (1,1,1)
  Fit = 0
  FitJoin = 0
  InnerFit = 0
  InnerFitJoin = 0
  InvalidShape = false
  Length = 5
  Length2 = 100
  Linearize = true
  NewSolid = false
  Profile = -> Export005
  Refine = true
  Suppress = false
  TaperInnerAngle = 0
  TaperInnerAngleRev = 0
  TreeRank = 431
  Type = 1
  ValidateShape = true
  _ProfileBasedVersion = 1
  _Version = 1
FEATURE [PartDesign::Pocket] Pocket023
  AddSubType = 1
  AutoTaperInnerAngle = false
  BaseFeature = -> Pocket022
  CheckUpToFaceLimits = true
  ClaimChildren = false
  Direction = (1,1,1)
  Fit = 0
  FitJoin = 0
  InnerFit = 0
  InnerFitJoin = 0
  InvalidShape = false
  Length = 12
  Length2 = 100
  Linearize = true
  NewSolid = false
  Profile = -> Export004
  Refine = true
  Suppress = false
  TaperInnerAngle = 0
  TaperInnerAngleRev = 0
  TreeRank = 432
  Type = 1
  ValidateShape = true
  _ProfileBasedVersion = 1
  _Version = 1
FEATURE [PartDesign::AuxGroup] Sketches
  Group = -> [Sketch042,Sketch043,Sketch044,Sketch045,Sketch047,Sketch048,Export004,Export005,Sketch049,Sketch050,Sketch051,Sketch052,Sketch061,Sketch062,Sketch063,Sketch070,Sketch079]
  TreeRank = 448
FEATURE [PartDesign::AuxGroup] Datums
  TreeRank = 449
FEATURE [PartDesign::AuxGroup] Misc
  Group = -> [Import004]
  TreeRank = 450
FEATURE [Sketcher::SketchObject] Sketch050
  ArcFitTolerance = 0
  AttachmentSupport = -> [XY_Plane024]
  ExternalBSplineMaxDegree = 0
  ExternalBSplineTolerance = 0
  ExternalGeometry = -> [Pocket023]
  FullyConstrained = true
  InternalTolerance = 1e-06
  InvalidShape = false
  MakeInternals = false
  MapMode = 5
  Placement = pos=(0,0,0) rot=(0,1,0;3.14159rad)
  Support = -> [XY_Plane024]
  TreeRank = 452
  ValidateShape = true
  sketch-geometry (10):
    g0: Circle [constr] CenterX=14.2396 CenterY=36.3363 CenterZ=0 NormalX=0 NormalY=0 NormalZ=1 AngleXU=0 Radius=3.5
    g1: Circle CenterX=14.2396 CenterY=36.3363 CenterZ=0 NormalX=0 NormalY=0 NormalZ=1 AngleXU=0 Radius=2.1
    g2: LineSegment [constr] StartX=0 StartY=39.8363 StartZ=0 EndX=14.2396 EndY=39.8363 EndZ=0
    g3: Circle CenterX=-38.588 CenterY=-5.83631 CenterZ=0 NormalX=0 NormalY=0 NormalZ=1 AngleXU=0 Radius=2.1
    g4: Circle CenterX=24.3484 CenterY=-30.5 CenterZ=0 NormalX=0 NormalY=0 NormalZ=1 AngleXU=0 Radius=2.1
    g5: LineSegment [constr] StartX=-38.588 StartY=-5.83631 StartZ=0 EndX=7.82e-14 EndY=-3.1584e-12 EndZ=0
    g6: LineSegment [constr] StartX=7.84e-14 StartY=-3.1586e-12 StartZ=0 EndX=14.2396 EndY=36.3363 EndZ=0
    g7: LineSegment [constr] StartX=7.84e-14 StartY=-3.1586e-12 StartZ=0 EndX=24.3484 EndY=-30.5 EndZ=0
    g8: LineSegment [constr] StartX=17.2707 StartY=38.0863 StartZ=0 EndX=39.2598 EndY=1.847e-13 EndZ=0
    g9: GeomPoint [constr] X=41.5692 Y=-4.45e-14 Z=0
  constraints (26):
    c: Coincident(g1,g0)
    c: Diameter(g0) = 7
    c: PointOnObject(g2,g-2)
    c: PointOnObject(g2,g0)
    c: Horizontal(g2)
    c: Tangent(g2,g0)
    c: DistanceY(g2,g-3) = 5
    c: Diameter(g1) = 4.2
    c: Equal(g4,g3)
    c: Equal(g3,g1)
    c: Coincident(g5,g3)
    c: Coincident(g5,g-1)
    c: Coincident(g6,g5)
    c: Coincident(g6,g1)
    c: Coincident(g7,g5)
    c: Coincident(g7,g4)
    c: Equal(g7,g5)
    c: Equal(g5,g6)
    c: Angle(g6,g5) = 2.0944
    c: Angle(g7,g6) = 2.0944
    c: PointOnObject(g8,g-1)
    c: Tangent(g8,g0) = 1.5708
    c: Parallel(g8,g-4)
    c: PointOnObject(g9,g-4)
    c: PointOnObject(g9,g-1)
    c: Distance(g8,g-4) = 2
FEATURE [PartDesign::Pocket] Pocket024
  AddSubType = 1
  AutoTaperInnerAngle = false
  BaseFeature = -> Pocket023
  CheckUpToFaceLimits = true
  ClaimChildren = false
  Direction = (1,1,1)
  Fit = 0
  FitJoin = 0
  InnerFit = 0
  InnerFitJoin = 0
  InvalidShape = false
  Length = 15
  Length2 = 100
  Linearize = true
  NewSolid = false
  Profile = -> Sketch050
  Refine = true
  Suppress = false
  TaperInnerAngle = 0
  TaperInnerAngleRev = 0
  TreeRank = 453
  Type = 0
  ValidateShape = true
  _ProfileBasedVersion = 1
  _Version = 1
FEATURE [Sketcher::SketchObject] Sketch051
  ArcFitTolerance = 0
  AttachmentSupport = -> [XY_Plane024]
  ExternalBSplineMaxDegree = 0
  ExternalBSplineTolerance = 0
  ExternalGeometry = -> [Pocket024]
  FullyConstrained = true
  InternalTolerance = 1e-06
  InvalidShape = false
  MakeInternals = false
  MapMode = 5
  Placement = pos=(0,0,0) rot=(0,1,0;3.14159rad)
  Support = -> [XY_Plane024]
  TreeRank = 454
  ValidateShape = true
  sketch-geometry (12):
    g0: LineSegment StartX=-40.6508 StartY=-2.40926 StartZ=0 EndX=-14.5283 EndY=42.8363 EndZ=0
    g1: LineSegment StartX=-14.5283 StartY=42.8363 StartZ=0 EndX=14.5283 EndY=42.8363 EndZ=0
    g2: LineSegment StartX=18.2389 StartY=36.4093 StartZ=0 EndX=44.3615 EndY=-8.83631 EndZ=0
    g3: LineSegment StartX=44.3615 StartY=-8.83631 StartZ=0 EndX=29.8332 EndY=-34 EndZ=0
    g4: LineSegment StartX=22.4119 StartY=-34 StartZ=0 EndX=-29.8332 EndY=-34 EndZ=0
    g5: LineSegment StartX=-44.3615 StartY=-8.83631 StartZ=0 EndX=-29.8332 EndY=-34 EndZ=0
    g6: LineSegment StartX=-44.3615 StartY=-8.83631 StartZ=0 EndX=-42.5873 EndY=-5.76336 EndZ=0
    g7: LineSegment StartX=29.8332 StartY=-34 StartZ=0 EndX=26.2849 EndY=-34 EndZ=0
    g8: LineSegment StartX=14.5283 StartY=42.8363 StartZ=0 EndX=16.3024 EndY=39.7634 EndZ=0
    g9: ArcOfCircle CenterX=-38.588 CenterY=-5.83631 CenterZ=0 NormalX=0 NormalY=0 NormalZ=1 AngleXU=0 Radius=4 StartAngle=3.12335 EndAngle=8.39582
    g10: ArcOfCircle CenterX=24.3484 CenterY=-30.5 CenterZ=0 NormalX=0 NormalY=0 NormalZ=1 AngleXU=0 Radius=4 StartAngle=5.21775 EndAngle=10.4902
    g11: ArcOfCircle CenterX=14.2396 CenterY=36.3363 CenterZ=0 NormalX=0 NormalY=0 NormalZ=1 AngleXU=0 Radius=4 StartAngle=1.02896 EndAngle=6.30142
  constraints (33):
    c: Coincident(g1,g0)
    c: Coincident(g3,g2)
    c: Horizontal(g4)
    c: Coincident(g5,g4)
    c: Equal(g5,g1)
    c: Equal(g1,g3)
    c: Equal(g0,g4)
    c: Equal(g4,g2)
    c: Horizontal(g1)
    c: DistanceY(g0,g-7) = 2
    c: Parallel(g0,g-6)
    c: Parallel(g5,g-8)
    c: Parallel(g2,g-9)
    c: Coincident(g6,g5)
    c: Coincident(g7,g3)
    c: Coincident(g8,g1)
    c: Tangent(g8,g2)
    c: Tangent(g7,g4)
    c: Tangent(g6,g0)
    c: Coincident(g9,g-4)
    c: Coincident(g9,g0)
    c: Coincident(g9,g6)
    c: Coincident(g10,g-5)
    c: Coincident(g10,g4)
    c: Coincident(g10,g7)
    c: Coincident(g11,g-3)
    c: Coincident(g11,g8)
    c: Coincident(g11,g2)
    c: Parallel(g3,g-10)
    c: Equal(g9,g10)
    c: Equal(g9,g11)
    c: Radius(g9) = 4
    c: DistanceY(g-11,g4) = 2
FEATURE [PartDesign::Pocket] Pocket025
  AddSubType = 1
  AutoTaperInnerAngle = false
  BaseFeature = -> Pocket024
  CheckUpToFaceLimits = true
  ClaimChildren = false
  Direction = (1,1,1)
  Fit = 0
  FitJoin = 0
  InnerFit = 0
  InnerFitJoin = 0
  InvalidShape = false
  Length = 39
  Length2 = 100
  Linearize = true
  NewSolid = false
  Profile = -> Sketch051
  Refine = true
  Suppress = false
  TaperInnerAngle = 0
  TaperInnerAngleRev = 0
  TreeRank = 455
  Type = 0
  ValidateShape = true
  _ProfileBasedVersion = 1
  _Version = 1
FEATURE [PartDesign::Fillet] Fillet013
  AddSubType = 0
  Base = -> Pocket025 [Edge104,Edge108,Edge114,Edge118,Edge102,Edge98,Edge112,Edge97,Edge110]
  BaseFeature = -> Pocket025
  InvalidShape = false
  NewSolid = false
  Radius = 1
  Refine = true
  SupportTransform = false
  Suppress = false
  TreeRank = 456
  UseAllEdges = false
  ValidateShape = true
FEATURE [PartDesign::Fillet] Fillet014
  AddSubType = 0
  Base = -> Fillet013 [Edge73,Edge55,Edge45]
  BaseFeature = -> Fillet013
  InvalidShape = false
  NewSolid = false
  Radius = 10
  Refine = true
  SupportTransform = false
  Suppress = false
  TreeRank = 457
  UseAllEdges = false
  ValidateShape = true
FEATURE [PartDesign::Fillet] Fillet015
  AddSubType = 0
  Base = -> Fillet014 [Edge98,Edge91,Edge92,Edge116,Edge104,Edge102,Edge100,Edge110,Edge112,Edge114]
  BaseFeature = -> Fillet014
  InvalidShape = false
  NewSolid = false
  Radius = 3
  Refine = true
  SupportTransform = false
  Suppress = false
  TreeRank = 458
  UseAllEdges = false
  ValidateShape = true
FEATURE [PartDesign::Pocket] Pocket026
  AddSubType = 1
  AutoTaperInnerAngle = false
  BaseFeature = -> Fillet015
  CheckUpToFaceLimits = true
  ClaimChildren = false
  Direction = (1,1,1)
  Fit = 0
  FitJoin = 0
  InnerFit = 0
  InnerFitJoin = 0
  InvalidShape = false
  Length = 5
  Length2 = 100
  Linearize = true
  NewSolid = false
  Profile = -> Sketch052
  Refine = true
  Reversed = true
  Suppress = false
  TaperInnerAngle = 0
  TaperInnerAngleRev = 0
  TreeRank = 460
  Type = 1
  ValidateShape = true
  _ProfileBasedVersion = 1
  _Version = 1
FEATURE [PartDesign::Fillet] Fillet016
  AddSubType = 0
  Base = -> Pocket026 [Edge237,Edge233,Edge226,Edge229,Edge230,Edge234]
  BaseFeature = -> Pocket026
  InvalidShape = false
  NewSolid = false
  Radius = 1
  Refine = true
  SupportTransform = false
  Suppress = false
  TreeRank = 461
  UseAllEdges = false
  ValidateShape = true
FEATURE [PartDesign::Chamfer] Chamfer002
  AddSubType = 0
  Angle = 45
  Base = -> Fillet016 [Face1]
  BaseFeature = -> Fillet016
  ChamferType = 0
  FlipDirection = false
  InvalidShape = false
  NewSolid = false
  Refine = true
  Size = 0.4
  Size2 = 1
  SupportTransform = false
  Suppress = false
  TreeRank = 462
  UseAllEdges = false
  ValidateShape = true
FEATURE [PartDesign::Chamfer] Chamfer003
  AddSubType = 0
  Angle = 45
  Base = -> Chamfer002 [Edge315,Edge309,Edge311]
  BaseFeature = -> Chamfer002
  ChamferType = 0
  FlipDirection = false
  InvalidShape = false
  NewSolid = false
  Refine = true
  Size = 1
  Size2 = 1
  SupportTransform = false
  Suppress = false
  TreeRank = 463
  UseAllEdges = false
  ValidateShape = true
FEATURE [PartDesign::Chamfer] Chamfer004
  AddSubType = 0
  Angle = 45
  Base = -> Chamfer003 [Edge187,Edge183]
  BaseFeature = -> Chamfer003
  ChamferType = 0
  FlipDirection = false
  InvalidShape = false
  NewSolid = false
  Refine = true
  Size = 0.4
  Size2 = 1
  SupportTransform = false
  Suppress = false
  TreeRank = 464
  UseAllEdges = false
  ValidateShape = true
FEATURE [PartDesign::Chamfer] Chamfer005
  AddSubType = 0
  Angle = 45
  Base = -> Chamfer004 [Edge292]
  BaseFeature = -> Chamfer004
  ChamferType = 0
  FlipDirection = false
  InvalidShape = false
  NewSolid = false
  Refine = true
  Size = 1
  Size2 = 1
  SupportTransform = false
  Suppress = false
  TreeRank = 465
  UseAllEdges = false
  ValidateShape = true
FEATURE [PartDesign::Chamfer] Chamfer006
  AddSubType = 0
  Angle = 45
  Base = -> Chamfer005 [Edge51]
  BaseFeature = -> Chamfer005
  ChamferType = 0
  FlipDirection = false
  InvalidShape = false
  NewSolid = false
  Refine = true
  Size = 1
  Size2 = 1
  SupportTransform = false
  Suppress = false
  TreeRank = 466
  UseAllEdges = false
  ValidateShape = true
FEATURE [PartDesign::Chamfer] Chamfer007
  AddSubType = 0
  Angle = 45
  Base = -> Chamfer006 [Edge257,Edge354]
  BaseFeature = -> Chamfer006
  ChamferType = 0
  FlipDirection = false
  InvalidShape = false
  NewSolid = false
  Refine = true
  Size = 0.4
  Size2 = 1
  SupportTransform = false
  Suppress = false
  TreeRank = 467
  UseAllEdges = false
  ValidateShape = true
FEATURE [PartDesign::Chamfer] Chamfer008
  AddSubType = 0
  Angle = 45
  Base = -> Chamfer007 [Edge60,Edge147,Edge58,Edge56,Edge146]
  BaseFeature = -> Chamfer007
  ChamferType = 0
  FlipDirection = false
  InvalidShape = false
  NewSolid = false
  Refine = true
  Size = 0.4
  Size2 = 1
  SupportTransform = false
  Suppress = false
  TreeRank = 468
  UseAllEdges = false
  ValidateShape = true
FEATURE [Sketcher::SketchObject] Sketch061
  ArcFitTolerance = 1e-06
  AttachmentSupport = -> [Chamfer008]
  ExternalBSplineMaxDegree = 0
  ExternalBSplineTolerance = 0
  ExternalGeometry = -> [Import004]
  FullyConstrained = true
  InternalTolerance = 1e-06
  InvalidShape = false
  MakeInternals = false
  MapMode = 5
  Placement = pos=(-1.29e-14,1.57e-14,56) rot=(0,0,1;0rad)
  Support = -> [Chamfer008]
  TreeRank = 632
  ValidateShape = true
  sketch-geometry (5):
    g0: ArcOfCircle CenterX=2.7639e-12 CenterY=-3.058e-13 CenterZ=0 NormalX=0 NormalY=0 NormalZ=1 AngleXU=0 Radius=39.1 StartAngle=5.32325 EndAngle=5.75959
    g1: ArcOfCircle CenterX=2.7639e-12 CenterY=-3.058e-13 CenterZ=0 NormalX=0 NormalY=0 NormalZ=1 AngleXU=0 Radius=46.8 StartAngle=5.32325 EndAngle=5.75959
    g2: LineSegment StartX=40.53 StartY=-23.4 StartZ=0 EndX=33.8616 EndY=-19.55 EndZ=0
    g3: LineSegment StartX=22.4268 StartY=-32.0288 StartZ=0 EndX=26.8434 EndY=-38.3363 EndZ=0
    g4: LineSegment [constr] StartX=2.7639e-12 StartY=-3.058e-13 StartZ=0 EndX=34.3752 EndY=-31.7582 EndZ=0
  constraints (15):
    c: Coincident(g0,g-1)
    c: Coincident(g1,g0)
    c: Coincident(g2,g1)
    c: Coincident(g2,g0)
    c: Coincident(g3,g0)
    c: Coincident(g3,g1)
    c: PointOnObject(g0,g2)
    c: PointOnObject(g0,g3)
    c: Radius(g0) = 39.1
    c: Radius(g1) = 46.8
    c: Angle(g2,g-1) = 0.523599
    c: Angle(g3,g-1) = 0.959931
    c: Coincident(g4,g0)
    c: PointOnObject(g4,g1)
    c: Distance(g4,g1) = 10
FEATURE [Sketcher::SketchObject] Sketch062
  ArcFitTolerance = 1e-06
  AttachmentSupport = -> [Chamfer008]
  ExternalBSplineMaxDegree = 0
  ExternalBSplineTolerance = 0
  ExternalGeometry = -> [Chamfer008]
  FullyConstrained = true
  InternalTolerance = 1e-06
  InvalidShape = false
  MakeInternals = false
  MapMode = 5
  Placement = pos=(0,0,39) rot=(1,0,0;3.14159rad)
  Support = -> [Chamfer008]
  TreeRank = 634
  ValidateShape = true
  sketch-geometry (7):
    g0: ArcOfCircle CenterX=-4.215e-13 CenterY=2.551e-13 CenterZ=0 NormalX=0 NormalY=0 NormalZ=1 AngleXU=0 Radius=32 StartAngle=0.64511 EndAngle=1.0821
    g1: LineSegment StartX=25.5691 StartY=19.2412 StartZ=0 EndX=33.6769 EndY=25.3425 EndZ=0
    g2: LineSegment StartX=17.5464 StartY=33 StartZ=0 EndX=15.0231 EndY=28.2543 EndZ=0
    g3: Circle [constr] CenterX=28.5788 CenterY=16.5 CenterZ=0 NormalX=0 NormalY=0 NormalZ=1 AngleXU=0 Radius=4
    g4: LineSegment StartX=17.5464 StartY=33 StartZ=0 EndX=24.0597 EndY=33 EndZ=0
    g5: LineSegment StartX=33.6769 StartY=25.3425 StartZ=0 EndX=31.8539 EndY=28.5 EndZ=0
    g6: ArcOfCircle CenterX=24.0597 CenterY=24 CenterZ=0 NormalX=0 NormalY=0 NormalZ=1 AngleXU=0 Radius=9 StartAngle=0.523599 EndAngle=1.5708
  constraints (18):
    c: Coincident(g0,g-1)
    c: Coincident(g1,g0)
    c: Coincident(g2,g0)
    c: PointOnObject(g0,g2)
    c: Radius(g0) = 32
    c: PointOnObject(g0,g1)
    c: Coincident(g3,g-5)
    c: Tangent(g3,g1)
    c: Diameter(g3) = 8
    c: Angle(g2,g-2) = 0.488692
    c: Coincident(g4,g2)
    c: Horizontal(g4)
    c: Coincident(g5,g1)
    c: Parallel(g5,g-3)
    c: Tangent(g6,g5) = -1.5708
    c: Tangent(g6,g4) = 1.5708
    c: Coincident(g6,g-4)
    c: DistanceY(g4,g-4) = 1
FEATURE [PartDesign::SubtractiveLoft] Loft
  AddSubType = 1
  BaseFeature = -> Chamfer008
  ClaimChildren = false
  Closed = false
  Fit = 0
  FitJoin = 1
  InnerFit = 0
  InnerFitJoin = 1
  InvalidShape = false
  Linearize = true
  MaxDegree = 5
  NewSolid = false
  Profile = -> Sketch061
  Refine = true
  Ruled = false
  Sections = -> [Sketch062]
  SplitProfile = false
  Suppress = false
  TreeRank = 635
  ValidateShape = true
  _ProfileBasedVersion = 1
FEATURE [Sketcher::SketchObject] Sketch063
  ArcFitTolerance = 1e-06
  AttachmentSupport = -> [Loft]
  ExternalBSplineMaxDegree = 0
  ExternalBSplineTolerance = 0
  ExternalGeometry = -> [Import004]
  FullyConstrained = true
  InternalTolerance = 1e-06
  InvalidShape = false
  MakeInternals = false
  MapMode = 5
  Placement = pos=(-1.29e-14,1.57e-14,56) rot=(0,0,1;0rad)
  Support = -> [Loft]
  TreeRank = 637
  ValidateShape = true
  sketch-geometry (6):
    g0: ArcOfCircle CenterX=-1.5419e-12 CenterY=-8.2642e-12 CenterZ=0 NormalX=0 NormalY=0 NormalZ=1 AngleXU=0 Radius=39.7306 StartAngle=5.88176 EndAngle=6.00393
    g1: ArcOfCircle CenterX=-1.5419e-12 CenterY=-8.2642e-12 CenterZ=0 NormalX=0 NormalY=0 NormalZ=1 AngleXU=0 Radius=47.3083 StartAngle=5.88176 EndAngle=6.00393
    g2: LineSegment StartX=38.1915 StartY=-10.9512 StartZ=0 EndX=45.4757 EndY=-13.0399 EndZ=0
    g3: LineSegment StartX=36.5722 StartY=-15.524 StartZ=0 EndX=43.5476 EndY=-18.4848 EndZ=0
    g4: Circle [constr] CenterX=38.9977 CenterY=-12.5932 CenterZ=0 NormalX=0 NormalY=0 NormalZ=1 AngleXU=0 Radius=1.25
    g5: Circle [constr] CenterX=42.9029 CenterY=-16.7545 CenterZ=0 NormalX=0 NormalY=0 NormalZ=1 AngleXU=0 Radius=1.25
  constraints (16):
    c: Coincident(g0,g-1)
    c: Coincident(g1,g0)
    c: Coincident(g2,g0)
    c: Coincident(g2,g1)
    c: Coincident(g3,g0)
    c: Coincident(g3,g1)
    c: PointOnObject(g0,g3)
    c: PointOnObject(g0,g2)
    c: Angle(g2,g-1) = 0.279253
    c: Angle(g3,g-1) = 0.401426
    c: Coincident(g4,g-3)
    c: Tangent(g4,g0)
    c: Coincident(g5,g-4)
    c: Tangent(g5,g1)
    c: Equal(g5,g4)
    c: Diameter(g5) = 2.5
FEATURE [PartDesign::Pocket] Pocket030
  AddSubType = 1
  AutoTaperInnerAngle = false
  BaseFeature = -> Loft
  CheckUpToFaceLimits = true
  ClaimChildren = false
  Direction = (1,1,1)
  Fit = 0
  FitJoin = 0
  InnerFit = 0
  InnerFitJoin = 0
  InvalidShape = false
  Length = 1
  Length2 = 100
  Linearize = true
  NewSolid = false
  Profile = -> Sketch063
  Refine = true
  Suppress = false
  TaperInnerAngle = 0
  TaperInnerAngleRev = 0
  TreeRank = 638
  Type = 0
  ValidateShape = true
  _ProfileBasedVersion = 1
  _Version = 1
FEATURE [PartDesign::Fillet] Fillet021
  AddSubType = 0
  Base = -> Pocket030 [Edge370,Edge368,Edge367,Edge372]
  BaseFeature = -> Pocket030
  InvalidShape = false
  NewSolid = false
  Radius = 0.5
  Refine = true
  SupportTransform = false
  Suppress = false
  TreeRank = 639
  UseAllEdges = false
  ValidateShape = true
FEATURE [PartDesign::Body] Body028  label="SupportLD06"
  AutoGroupSolids = false
  ClaimAllChildren = false
  ExportMode = 0
  Group = -> [ShapeBinder,Sketch064,Pad033,Fillet022,Sketch065,Import005,Pocket031]
  InvalidShape = false
  Origin = -> Origin054
  Placement = pos=(0,0,3) rot=(0,0,1;0rad)
  SingleSolid = true
  Tip = -> Pocket031
  TreeRank = 649
  ValidateShape = true
  _ExportChildren = -> [ShapeBinder,Pad033,Fillet022,Import005,Pocket031]
  _GroupVersion = 1
FEATURE [PartDesign::ShapeBinder] ShapeBinder
  InvalidShape = false
  Support = -> [Fillet021]
  TraceSupport = false
  TreeRank = 650
  ValidateShape = true
FEATURE [Sketcher::SketchObject] Sketch064
  ArcFitTolerance = 1e-06
  AttachmentSupport = -> [ShapeBinder]
  ExternalBSplineMaxDegree = 0
  ExternalBSplineTolerance = 0
  ExternalGeometry = -> [ShapeBinder]
  FullyConstrained = true
  InternalTolerance = 1e-06
  InvalidShape = false
  MakeInternals = false
  MapMode = 5
  Placement = pos=(-1e-14,1.31e-14,45.3) rot=(0,0,1;0rad)
  Support = -> [ShapeBinder]
  TreeRank = 651
  ValidateShape = true
  sketch-geometry (20):
    g0: Circle CenterX=-25.9808 CenterY=15 CenterZ=0 NormalX=0 NormalY=0 NormalZ=1 AngleXU=0 Radius=1.6
    g1: Circle CenterX=15 CenterY=25.9808 CenterZ=0 NormalX=0 NormalY=0 NormalZ=1 AngleXU=0 Radius=1.6
    g2: ArcOfCircle CenterX=28.5788 CenterY=-16.5 CenterZ=0 NormalX=0 NormalY=0 NormalZ=1 AngleXU=0 Radius=6 StartAngle=1.8551 EndAngle=3.38089
    g3: ArcOfCircle CenterX=-28.5788 CenterY=-16.5 CenterZ=0 NormalX=0 NormalY=0 NormalZ=1 AngleXU=0 Radius=6 StartAngle=6.04389 EndAngle=7.56968
    g4: ArcOfCircle CenterX=6.5275e-12 CenterY=33 CenterZ=0 NormalX=0 NormalY=0 NormalZ=1 AngleXU=0 Radius=6 StartAngle=3.94949 EndAngle=5.47528
    g5: ArcOfCircle CenterX=1.6239e-11 CenterY=6.14944e-11 CenterZ=0 NormalX=0 NormalY=0 NormalZ=1 AngleXU=0 Radius=32.5 StartAngle=5.98591 EndAngle=7.62766
    g6: ArcOfCircle CenterX=1.6239e-11 CenterY=6.14944e-11 CenterZ=0 NormalX=0 NormalY=0 NormalZ=1 AngleXU=0 Radius=32.5 StartAngle=3.89151 EndAngle=5.53326
    g7: ArcOfCircle CenterX=1.6239e-11 CenterY=6.14944e-11 CenterZ=0 NormalX=0 NormalY=0 NormalZ=1 AngleXU=0 Radius=32.5 StartAngle=1.79712 EndAngle=3.43887
    g8: LineSegment StartX=-4.1461 StartY=28.663 StartZ=0 EndX=-7.29285 EndY=31.6712 EndZ=0
    g9: LineSegment StartX=4.1461 StartY=28.663 StartZ=0 EndX=7.29285 EndY=31.6712 EndZ=0
    g10: LineSegment StartX=26.8959 StartY=-10.7409 StartZ=0 EndX=31.0745 EndY=-9.5198 EndZ=0
    g11: LineSegment StartX=22.7498 StartY=-17.9221 StartZ=0 EndX=23.7816 EndY=-22.1514 EndZ=0
    g12: LineSegment StartX=-23.7816 StartY=-22.1514 StartZ=0 EndX=-22.7498 EndY=-17.9221 EndZ=0
    g13: LineSegment StartX=-31.0745 StartY=-9.5198 StartZ=0 EndX=-26.8959 EndY=-10.7409 EndZ=0
    g14: ArcOfCircle CenterX=-17.0875 CenterY=-19.5964 CenterZ=0 NormalX=0 NormalY=0 NormalZ=1 AngleXU=0 Radius=4 StartAngle=1.0472 EndAngle=4.18879
    g15: ArcOfCircle CenterX=-8.42722 CenterY=-24.5964 CenterZ=0 NormalX=0 NormalY=0 NormalZ=1 AngleXU=0 Radius=4 StartAngle=4.18879 EndAngle=7.33038
    g16: LineSegment StartX=-19.0875 StartY=-23.0605 StartZ=0 EndX=-10.4272 EndY=-28.0605 EndZ=0
    g17: LineSegment StartX=-6.42722 StartY=-21.1323 StartZ=0 EndX=-15.0875 EndY=-16.1323 EndZ=0
    g18: LineSegment [constr] StartX=-17.0875 StartY=-19.5964 StartZ=0 EndX=-8.42722 EndY=-24.5964 EndZ=0
    g19: LineSegment [constr] StartX=-12.7574 StartY=-22.0964 StartZ=0 EndX=1.62395e-11 EndY=6.14939e-11 EndZ=0
  constraints (48):
    c: Coincident(g0,g-4)
    c: Coincident(g1,g-3)
    c: Equal(g1,g0)
    c: Diameter(g1) = 3.2
    c: Coincident(g2,g-6)
    c: Coincident(g3,g-7)
    c: Coincident(g4,g-5)
    c: Coincident(g5,g-10)
    c: Coincident(g6,g5)
    c: Coincident(g7,g5)
    c: Equal(g5,g7)
    c: Equal(g7,g6)
    c: Equal(g4,g2)
    c: Equal(g2,g3)
    c: Tangent(g-3,g5)
    c: Coincident(g8,g7)
    c: Coincident(g9,g5)
    c: Coincident(g10,g5)
    c: Coincident(g11,g6)
    c: Coincident(g12,g6)
    c: Coincident(g13,g7)
    c: Tangent(g13,g3) = 1.5708
    c: Tangent(g12,g3) = -1.5708
    c: Tangent(g11,g2) = -1.5708
    c: Tangent(g10,g2) = 1.5708
    c: Tangent(g9,g4) = -1.5708
    c: Tangent(g8,g4) = 1.5708
    c: Equal(g13,g12)
    c: Equal(g12,g11)
    c: Equal(g11,g10)
    c: Equal(g10,g9)
    c: Equal(g9,g8)
    c: Radius(g4) = 6
    c: PointOnObject(g-9,g9)
    c: Tangent(g14,g16) = -1.5708
    c: Tangent(g16,g15) = -1.5708
    c: Tangent(g15,g17) = -1.5708
    c: Tangent(g17,g14) = -1.5708
    c: Equal(g14,g15)
    c: Tangent(g15,g-11)
    c: Coincident(g18,g14)
    c: Coincident(g18,g15)
    c: Coincident(g19,g5)
    c: Symmetric(g14,g15,g19)
    c: Perpendicular(g19,g18)
    c: Radius(g15) = 4
    c: Distance(g17) = 10
    c: Angle(g-2,g19) = 2.61799
FEATURE [PartDesign::Pad] Pad033
  AddSubType = 0
  AlongSketchNormal = false
  AutoTaperInnerAngle = false
  CheckUpToFaceLimits = true
  ClaimChildren = false
  Direction = (-2e-16,3e-16,1)
  Fit = 0
  FitJoin = 0
  InnerFit = 0
  InnerFitJoin = 0
  InvalidShape = false
  Length = 3
  Length2 = 100
  Linearize = true
  NewSolid = false
  Profile = -> Sketch064
  Refine = true
  Suppress = false
  TaperInnerAngle = 0
  TaperInnerAngleRev = 0
  TreeRank = 652
  Type = 0
  ValidateShape = true
  _ProfileBasedVersion = 1
FEATURE [PartDesign::Fillet] Fillet022
  AddSubType = 0
  Base = -> Pad033 [Edge11,Edge20,Edge2,Edge8,Edge32,Edge23]
  BaseFeature = -> Pad033
  InvalidShape = false
  NewSolid = false
  Radius = 2
  Refine = true
  SupportTransform = false
  Suppress = false
  TreeRank = 653
  UseAllEdges = false
  ValidateShape = true
FEATURE [Sketcher::SketchObject] Sketch065
  ArcFitTolerance = 1e-06
  AttachmentSupport = -> [Fillet022]
  ExternalBSplineMaxDegree = 0
  ExternalBSplineTolerance = 0
  ExternalGeometry = -> [Import005]
  FullyConstrained = true
  InternalTolerance = 1e-06
  InvalidShape = false
  MakeInternals = false
  MapMode = 5
  Placement = pos=(-1.09e-14,1.36e-14,45.3) rot=(1,0,0;3.14159rad)
  Support = -> [Fillet022]
  TreeRank = 654
  ValidateShape = true
  sketch-geometry (9):
    g0: Circle CenterX=-19.261 CenterY=5.16096 CenterZ=0 NormalX=0 NormalY=0 NormalZ=1 AngleXU=0 Radius=1.6
    g1: Circle CenterX=19.261 CenterY=-5.16096 CenterZ=0 NormalX=0 NormalY=0 NormalZ=1 AngleXU=0 Radius=1.6
    g2: LineSegment [constr] StartX=19.261 StartY=-5.16096 StartZ=0 EndX=5.16096 EndY=19.261 EndZ=0
    g3: LineSegment [constr] StartX=5.16096 StartY=19.261 StartZ=0 EndX=-19.261 EndY=5.16096 EndZ=0
    g4: LineSegment [constr] StartX=-19.261 StartY=5.16096 StartZ=0 EndX=-5.16096 EndY=-19.261 EndZ=0
    g5: LineSegment [constr] StartX=-5.16096 StartY=-19.261 StartZ=0 EndX=19.261 EndY=-5.16096 EndZ=0
    g6: GeomPoint [constr] X=0 Y=0 Z=0
    g7: Circle CenterX=5.16096 CenterY=19.261 CenterZ=0 NormalX=0 NormalY=0 NormalZ=1 AngleXU=0 Radius=1.6
    g8: Circle CenterX=-5.16096 CenterY=-19.261 CenterZ=0 NormalX=0 NormalY=0 NormalZ=1 AngleXU=0 Radius=1.6
  constraints (19):
    c: Coincident(g2,g3)
    c: Coincident(g3,g4)
    c: Coincident(g4,g5)
    c: Coincident(g5,g2)
    c: Parallel(g3,g5)
    c: Parallel(g2,g4)
    c: Symmetric(g3,g2,g6)
    c: Coincident(g6,g-1)
    c: Perpendicular(g2,g3)
    c: Coincident(g0,g3)
    c: Equal(g2,g3)
    c: Coincident(g7,g2)
    c: Coincident(g8,g4)
    c: Equal(g8,g0)
    c: Equal(g0,g7)
    c: Equal(g7,g1)
    c: Diameter(g0) = 3.2
    c: Coincident(g2,g-3)
    c: Coincident(g1,g2)
FEATURE [PartDesign::Pocket] Pocket031
  AddSubType = 1
  AutoTaperInnerAngle = false
  BaseFeature = -> Fillet022
  CheckUpToFaceLimits = true
  ClaimChildren = false
  Direction = (-2e-16,3e-16,1)
  Fit = 0
  FitJoin = 0
  InnerFit = 0
  InnerFitJoin = 0
  InvalidShape = false
  Length = 5
  Length2 = 100
  Linearize = true
  NewSolid = false
  Profile = -> Sketch065
  Refine = true
  Suppress = false
  TaperInnerAngle = 0
  TaperInnerAngleRev = 0
  TreeRank = 656
  Type = 1
  ValidateShape = true
  _ProfileBasedVersion = 1
  _Version = 1
FEATURE [Sketcher::SketchObject] Sketch070
  ArcFitTolerance = 1e-06
  AttachmentSupport = -> [XY_Plane024]
  ExternalBSplineMaxDegree = 0
  ExternalBSplineTolerance = 0
  ExternalGeometry = -> [Fillet021]
  FullyConstrained = true
  InternalTolerance = 1e-06
  InvalidShape = false
  MakeInternals = false
  MapMode = 5
  Placement = pos=(0,0,0) rot=(0,1,0;3.14159rad)
  Support = -> [XY_Plane024]
  TreeRank = 720
  ValidateShape = true
  sketch-geometry (11):
    g0: LineSegment StartX=24.8288 StartY=22.9952 StartZ=0 EndX=27.4269 EndY=24.4952 EndZ=0
    g1: LineSegment StartX=27.4269 StartY=24.4952 StartZ=0 EndX=34.9269 EndY=11.5048 EndZ=0
    g2: LineSegment StartX=34.9269 StartY=11.5048 StartZ=0 EndX=32.3288 EndY=10.0048 EndZ=0
    g3: LineSegment StartX=32.3288 StartY=10.0048 StartZ=0 EndX=24.8288 EndY=22.9952 EndZ=0
    g4: GeomPoint [constr] X=31.1769 Y=18 Z=0
    g5: LineSegment StartX=37.909 StartY=10.3397 StartZ=0 EndX=36.1769 EndY=9.33975 EndZ=0
    g6: LineSegment StartX=26.1769 StartY=26.6603 StartZ=0 EndX=27.909 EndY=27.6603 EndZ=0
    g7: LineSegment StartX=27.909 StartY=27.6603 StartZ=0 EndX=37.909 EndY=10.3397 EndZ=0
    g8: LineSegment StartX=26.1769 StartY=26.6603 StartZ=0 EndX=24.4449 EndY=25.6603 EndZ=0
    g9: LineSegment StartX=24.4449 StartY=25.6603 StartZ=0 EndX=34.4449 EndY=8.33975 EndZ=0
    g10: LineSegment StartX=34.4449 StartY=8.33975 StartZ=0 EndX=36.1769 EndY=9.33975 EndZ=0
  constraints (27):
    c: Coincident(g0,g1)
    c: Coincident(g1,g2)
    c: Coincident(g2,g3)
    c: Coincident(g3,g0)
    c: Parallel(g0,g2)
    c: Parallel(g1,g3)
    c: Perpendicular(g1,g0)
    c: PointOnObject(g1,g-3)
    c: Distance(g2) = 3
    c: Distance(g1) = 15
    c: Symmetric(g0,g1,g4)
    c: Symmetric(g-3,g-3,g4)
    c: Coincident(g6,g7)
    c: Coincident(g7,g5)
    c: Parallel(g5,g6)
    c: PointOnObject(g6,g-3)
    c: Symmetric(g6,g5,g4)
    c: Distance(g6) = 2
    c: Distance(g7) = 20
    c: Perpendicular(g6,g7)
    c: PointOnObject(g8,g-4)
    c: Coincident(g9,g8)
    c: PointOnObject(g9,g-4)
    c: Coincident(g10,g9)
    c: Tangent(g10,g5) = 1.5708
    c: Tangent(g8,g6) = 1.5708
    c: Parallel(g7,g9)
FEATURE [App::Part] Part007  label="BeaconAssembled"
  ClaimAllChildren = false
  ExportMode = 1
  Group = -> [Body023,Body024,MatDetection_2023_1,Part006,Body028,Group006,Screw,Screw001,PcbStandoff002,PcbStandoff,PcbStandoff001,Link001,Body,Body029,Body031,Body033,Body034]
  Origin = -> Origin061
  TreeRank = 819
  _ExportChildren = -> [Body023,Body024,MatDetection_2023_1,Part006,Body028,Group006,Link001,Body,Body029,Body031,Body033,Body034]
  _GroupVersion = 1
FEATURE [Sketcher::SketchObject] Sketch079
  ArcFitTolerance = 1e-06
  AttachmentSupport = -> [Fillet021]
  ExternalBSplineMaxDegree = 5
  ExternalBSplineTolerance = 0.0001
  FullyConstrained = true
  InternalTolerance = 1e-06
  InvalidShape = false
  MakeInternals = true
  MapMode = 5
  Placement = pos=(-31.1769,18,0) rot=(-0.377964,0.654654,0.654654;3.86433rad)
  Support = -> [Fillet021]
  TreeRank = 825
  ValidateShape = false
  sketch-geometry (5):
    g0: LineSegment StartX=-20 StartY=1 StartZ=0 EndX=-20 EndY=35 EndZ=0
    g1: LineSegment StartX=-20 StartY=35 StartZ=0 EndX=20 EndY=35 EndZ=0
    g2: LineSegment StartX=20 StartY=35 StartZ=0 EndX=20 EndY=1 EndZ=0
    g3: LineSegment StartX=20 StartY=1 StartZ=0 EndX=-20 EndY=1 EndZ=0
    g4: GeomPoint [constr] X=0 Y=18 Z=0
  constraints (13):
    c: Coincident(g0,g1)
    c: Coincident(g1,g2)
    c: Coincident(g2,g3)
    c: Coincident(g3,g0)
    c: Horizontal(g1)
    c: Horizontal(g3)
    c: Vertical(g0)
    c: Vertical(g2)
    c: Symmetric(g1,g0,g4)
    c: PointOnObject(g4,g-2)
    c: DistanceY(g-1,g2) = 1
    c: DistanceY(g2,g2) = 34
    c: DistanceX(g1,g1) = 40
FEATURE [PartDesign::Pad] Pad041
  AddSubType = 0
  AlongSketchNormal = false
  AutoTaperInnerAngle = true
  BaseFeature = -> Fillet021
  CheckUpToFaceLimits = true
  ClaimChildren = false
  Direction = (-0.866025,0.5,0)
  Fit = 0
  FitJoin = 0
  InnerFit = 0
  InnerFitJoin = 0
  InvalidShape = true
  Length = 2
  Length2 = 10
  Linearize = true
  NewSolid = false
  Profile = -> Sketch079
  ReferenceAxis = -> Sketch079 [N_Axis]
  Refine = true
  Reversed = true
  Suppress = false
  TaperInnerAngle = 0
  TaperInnerAngleRev = 0
  TreeRank = 826
  Type = 0
  ValidateShape = true
  _ProfileBasedVersion = 1
note: 1 file-system path scrubbed to <path> (originals preserved in the JSON sidecar)

RESOLVED EXTERNAL PARTS (link-assembly join: the EXTERNAL_REF files above that resolve inside this repo's crawl, each included once):
---- part ../mechanical-parts/generic-hardware.FCStd = doc fcstd_c3dd29bfd943 (311813 chars; too large to inline — full recipe in that document) ----
